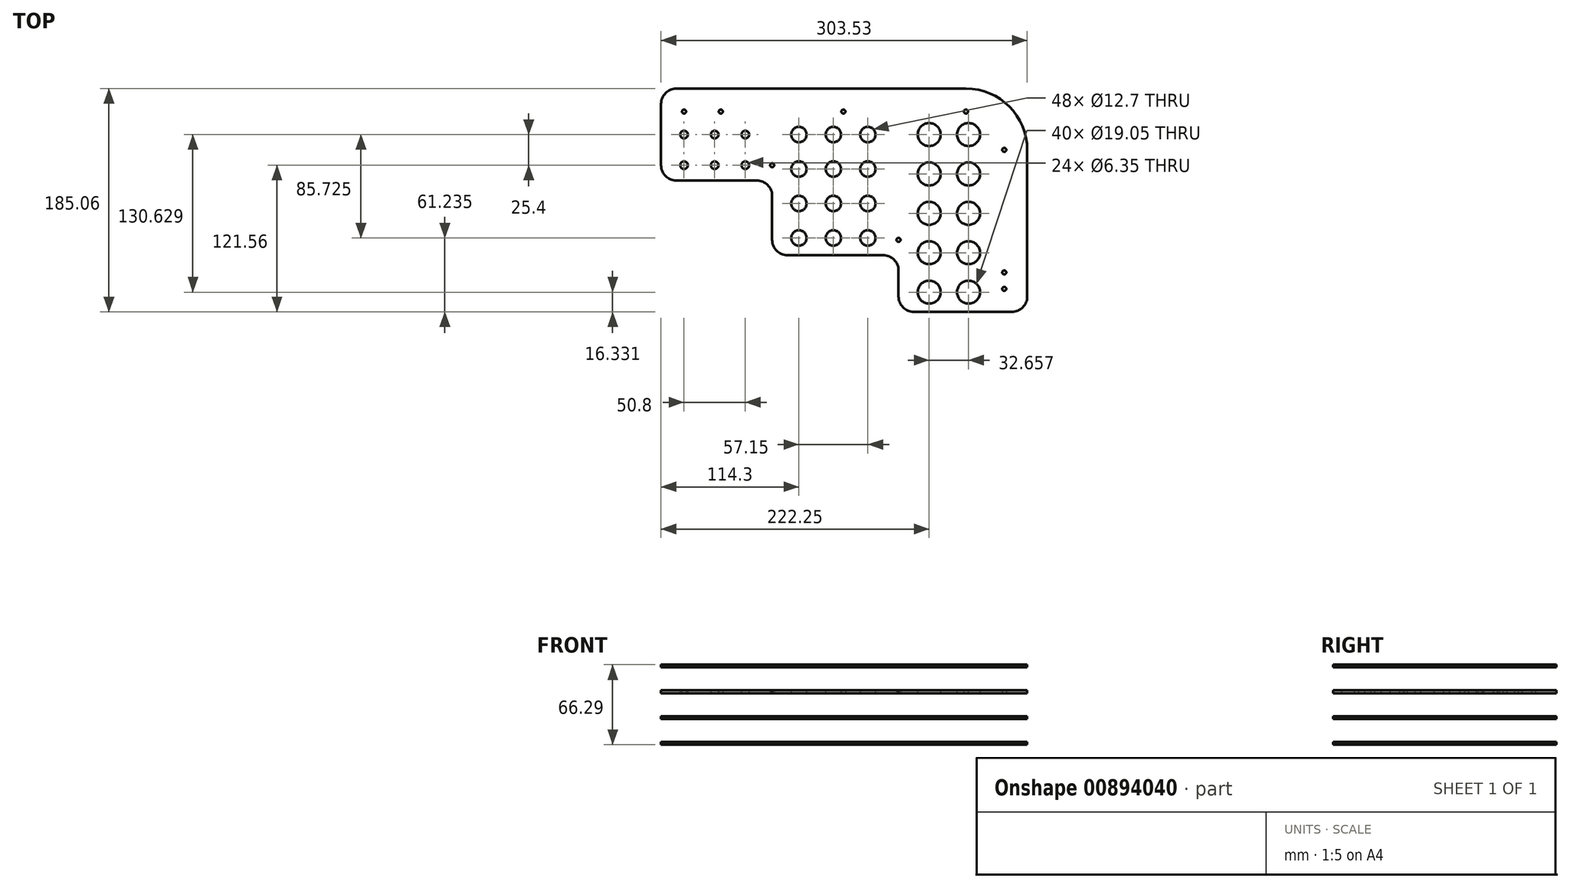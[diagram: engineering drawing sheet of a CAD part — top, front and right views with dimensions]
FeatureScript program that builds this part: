
annotation { "Feature Type Name" : "Feature", "Feature Type Description" : "" }
export const myFeature = defineFeature(function(context is Context, id is Id, definition is map)
    precondition{}
    {
        {
            var Q0;
            Q0=qCreatedBy(makeId("Top.planeOp"),FACE);
            var sketch = newSketch(context, id + "F0", { "sketchPlane" : qUnion([Q0])});
            skCircle(sketch, "E0", {"center": v(38.1, 38.1) * mm, "radius": 1.59 * mm});
            skCircle(sketch, "E1.0.1.0", {"center": v(38.1, 60.96) * mm, "radius": 1.59 * mm});
            skCircle(sketch, "E1.0.2.0", {"center": v(38.1, 83.82) * mm, "radius": 1.59 * mm});
            skCircle(sketch, "E1.0.3.0", {"center": v(38.1, 106.68) * mm, "radius": 1.59 * mm});
            skCircle(sketch, "E1.0.4.0", {"center": v(38.1, 129.54) * mm, "radius": 1.59 * mm});
            skCircle(sketch, "E1.0.5.0", {"center": v(38.1, 152.4) * mm, "radius": 1.59 * mm});
            skCircle(sketch, "E1.0.6.0", {"center": v(38.1, 175.26) * mm, "radius": 1.59 * mm});
            skCircle(sketch, "E1.0.7.0", {"center": v(38.1, 198.12) * mm, "radius": 1.59 * mm});
            skLineSegment(sketch, "E1.direction1", {"start": v(38.1, 38.1) * mm, "end": v(60.96, 38.1) * mm, "construction": true});
            skLineSegment(sketch, "E1.direction2", {"start": v(38.1, 38.1) * mm, "end": v(38.1, 60.96) * mm, "construction": true});
            skLineSegment(sketch, "E2.bottom", {"start": v(50.8, 304.8) * mm, "end": v(355.6, 304.8) * mm});
            skLineSegment(sketch, "E2.top", {"start": v(50.8, 0) * mm, "end": v(355.6, 0) * mm});
            skLineSegment(sketch, "E2.left", {"start": v(0, 254) * mm, "end": v(0, 50.8) * mm});
            skLineSegment(sketch, "E2.right", {"start": v(406.4, 254) * mm, "end": v(406.4, 50.8) * mm});
            skLineSegment(sketch, "E3.0", {"start": v(38.1, 266.7) * mm, "end": v(38.1, 38.1) * mm, "construction": true});
            skLineSegment(sketch, "E3.1", {"start": v(38.1, 266.7) * mm, "end": v(368.3, 266.7) * mm, "construction": true});
            skLineSegment(sketch, "E3.2", {"start": v(368.3, 266.7) * mm, "end": v(368.3, 38.1) * mm, "construction": true});
            skLineSegment(sketch, "E3.3", {"start": v(38.1, 38.1) * mm, "end": v(368.3, 38.1) * mm, "construction": true});
            skCircle(sketch, "E4.0.0.8", {"center": v(38.1, 220.98) * mm, "radius": 1.59 * mm});
            skCircle(sketch, "E4.0.0.9", {"center": v(38.1, 243.84) * mm, "radius": 1.59 * mm});
            skCircle(sketch, "E5.0.1.0", {"center": v(60.96, 38.1) * mm, "radius": 1.59 * mm});
            skCircle(sketch, "E5.0.1.1", {"center": v(60.96, 60.96) * mm, "radius": 1.59 * mm});
            skCircle(sketch, "E5.0.1.2", {"center": v(60.96, 83.82) * mm, "radius": 1.59 * mm});
            skCircle(sketch, "E5.0.1.3", {"center": v(60.96, 106.68) * mm, "radius": 1.59 * mm});
            skCircle(sketch, "E5.0.1.4", {"center": v(60.96, 129.54) * mm, "radius": 1.59 * mm});
            skCircle(sketch, "E5.0.1.5", {"center": v(60.96, 152.4) * mm, "radius": 1.59 * mm});
            skCircle(sketch, "E5.0.1.6", {"center": v(60.96, 175.26) * mm, "radius": 1.59 * mm});
            skCircle(sketch, "E5.0.1.7", {"center": v(60.96, 198.12) * mm, "radius": 1.59 * mm});
            skCircle(sketch, "E5.0.1.8", {"center": v(60.96, 220.98) * mm, "radius": 1.59 * mm});
            skCircle(sketch, "E5.0.1.9", {"center": v(60.96, 243.84) * mm, "radius": 1.59 * mm});
            skCircle(sketch, "E5.0.2.0", {"center": v(83.82, 38.1) * mm, "radius": 1.59 * mm});
            skCircle(sketch, "E5.0.2.1", {"center": v(83.82, 60.96) * mm, "radius": 1.59 * mm});
            skCircle(sketch, "E5.0.2.2", {"center": v(83.82, 83.82) * mm, "radius": 1.59 * mm});
            skCircle(sketch, "E5.0.2.3", {"center": v(83.82, 106.68) * mm, "radius": 1.59 * mm});
            skCircle(sketch, "E5.0.2.4", {"center": v(83.82, 129.54) * mm, "radius": 1.59 * mm});
            skCircle(sketch, "E5.0.2.5", {"center": v(83.82, 152.4) * mm, "radius": 1.59 * mm});
            skCircle(sketch, "E5.0.2.6", {"center": v(83.82, 175.26) * mm, "radius": 1.59 * mm});
            skCircle(sketch, "E5.0.2.7", {"center": v(83.82, 198.12) * mm, "radius": 1.59 * mm});
            skCircle(sketch, "E5.0.2.8", {"center": v(83.82, 220.98) * mm, "radius": 1.59 * mm});
            skCircle(sketch, "E5.0.2.9", {"center": v(83.82, 243.84) * mm, "radius": 1.59 * mm});
            skCircle(sketch, "E6.0.0.10", {"center": v(38.1, 266.7) * mm, "radius": 1.59 * mm});
            skCircle(sketch, "E6.0.1.10", {"center": v(60.96, 266.7) * mm, "radius": 1.59 * mm});
            skCircle(sketch, "E6.0.2.10", {"center": v(83.82, 266.7) * mm, "radius": 1.59 * mm});
            skCircle(sketch, "E7", {"center": v(121.92, 38.1) * mm, "radius": 3.18 * mm});
            skCircle(sketch, "E8.0.1.0", {"center": v(121.92, 63.5) * mm, "radius": 3.18 * mm});
            skCircle(sketch, "E8.0.2.0", {"center": v(121.92, 88.9) * mm, "radius": 3.18 * mm});
            skCircle(sketch, "E8.0.3.0", {"center": v(121.92, 114.3) * mm, "radius": 3.18 * mm});
            skCircle(sketch, "E8.0.4.0", {"center": v(121.92, 139.7) * mm, "radius": 3.18 * mm});
            skCircle(sketch, "E8.0.5.0", {"center": v(121.92, 165.1) * mm, "radius": 3.18 * mm});
            skCircle(sketch, "E8.0.6.0", {"center": v(121.92, 190.5) * mm, "radius": 3.18 * mm});
            skCircle(sketch, "E8.0.7.0", {"center": v(121.92, 215.9) * mm, "radius": 3.18 * mm});
            skCircle(sketch, "E8.0.8.0", {"center": v(121.92, 241.3) * mm, "radius": 3.18 * mm});
            skCircle(sketch, "E8.0.9.0", {"center": v(121.92, 266.7) * mm, "radius": 3.18 * mm});
            skCircle(sketch, "E8.1.0.0", {"center": v(147.32, 38.1) * mm, "radius": 3.18 * mm});
            skCircle(sketch, "E8.1.1.0", {"center": v(147.32, 63.5) * mm, "radius": 3.18 * mm});
            skCircle(sketch, "E8.1.2.0", {"center": v(147.32, 88.9) * mm, "radius": 3.18 * mm});
            skCircle(sketch, "E8.1.3.0", {"center": v(147.32, 114.3) * mm, "radius": 3.18 * mm});
            skCircle(sketch, "E8.1.4.0", {"center": v(147.32, 139.7) * mm, "radius": 3.18 * mm});
            skCircle(sketch, "E8.1.5.0", {"center": v(147.32, 165.1) * mm, "radius": 3.18 * mm});
            skCircle(sketch, "E8.1.6.0", {"center": v(147.32, 190.5) * mm, "radius": 3.18 * mm});
            skCircle(sketch, "E8.1.7.0", {"center": v(147.32, 215.9) * mm, "radius": 3.18 * mm});
            skCircle(sketch, "E8.1.8.0", {"center": v(147.32, 241.3) * mm, "radius": 3.18 * mm});
            skCircle(sketch, "E8.1.9.0", {"center": v(147.32, 266.7) * mm, "radius": 3.18 * mm});
            skCircle(sketch, "E8.2.0.0", {"center": v(172.72, 38.1) * mm, "radius": 3.18 * mm});
            skCircle(sketch, "E8.2.1.0", {"center": v(172.72, 63.5) * mm, "radius": 3.18 * mm});
            skCircle(sketch, "E8.2.2.0", {"center": v(172.72, 88.9) * mm, "radius": 3.18 * mm});
            skCircle(sketch, "E8.2.3.0", {"center": v(172.72, 114.3) * mm, "radius": 3.18 * mm});
            skCircle(sketch, "E8.2.4.0", {"center": v(172.72, 139.7) * mm, "radius": 3.18 * mm});
            skCircle(sketch, "E8.2.5.0", {"center": v(172.72, 165.1) * mm, "radius": 3.18 * mm});
            skCircle(sketch, "E8.2.6.0", {"center": v(172.72, 190.5) * mm, "radius": 3.18 * mm});
            skCircle(sketch, "E8.2.7.0", {"center": v(172.72, 215.9) * mm, "radius": 3.18 * mm});
            skCircle(sketch, "E8.2.8.0", {"center": v(172.72, 241.3) * mm, "radius": 3.18 * mm});
            skCircle(sketch, "E8.2.9.0", {"center": v(172.72, 266.7) * mm, "radius": 3.18 * mm});
            skLineSegment(sketch, "E8.direction1", {"start": v(121.92, 38.1) * mm, "end": v(147.32, 38.1) * mm, "construction": true});
            skLineSegment(sketch, "E8.direction2", {"start": v(121.92, 38.1) * mm, "end": v(121.92, 63.5) * mm, "construction": true});
            skCircle(sketch, "E9", {"center": v(217.17, 38.1) * mm, "radius": 6.35 * mm});
            skCircle(sketch, "E10.0.1.0", {"center": v(217.17, 66.67) * mm, "radius": 6.35 * mm});
            skCircle(sketch, "E10.0.2.0", {"center": v(217.17, 95.25) * mm, "radius": 6.35 * mm});
            skCircle(sketch, "E10.0.3.0", {"center": v(217.17, 123.82) * mm, "radius": 6.35 * mm});
            skCircle(sketch, "E10.0.4.0", {"center": v(217.17, 152.4) * mm, "radius": 6.35 * mm});
            skCircle(sketch, "E10.0.5.0", {"center": v(217.17, 180.97) * mm, "radius": 6.35 * mm});
            skCircle(sketch, "E10.0.6.0", {"center": v(217.17, 209.55) * mm, "radius": 6.35 * mm});
            skCircle(sketch, "E10.0.7.0", {"center": v(217.17, 238.12) * mm, "radius": 6.35 * mm});
            skCircle(sketch, "E10.0.8.0", {"center": v(217.17, 266.7) * mm, "radius": 6.35 * mm});
            skCircle(sketch, "E10.1.0.0", {"center": v(245.74, 38.1) * mm, "radius": 6.35 * mm});
            skCircle(sketch, "E10.1.1.0", {"center": v(245.74, 66.67) * mm, "radius": 6.35 * mm});
            skCircle(sketch, "E10.1.2.0", {"center": v(245.74, 95.25) * mm, "radius": 6.35 * mm});
            skCircle(sketch, "E10.1.3.0", {"center": v(245.74, 123.82) * mm, "radius": 6.35 * mm});
            skCircle(sketch, "E10.1.4.0", {"center": v(245.74, 152.4) * mm, "radius": 6.35 * mm});
            skCircle(sketch, "E10.1.5.0", {"center": v(245.74, 180.97) * mm, "radius": 6.35 * mm});
            skCircle(sketch, "E10.1.6.0", {"center": v(245.74, 209.55) * mm, "radius": 6.35 * mm});
            skCircle(sketch, "E10.1.7.0", {"center": v(245.74, 238.12) * mm, "radius": 6.35 * mm});
            skCircle(sketch, "E10.1.8.0", {"center": v(245.74, 266.7) * mm, "radius": 6.35 * mm});
            skCircle(sketch, "E10.2.0.0", {"center": v(274.32, 38.1) * mm, "radius": 6.35 * mm});
            skCircle(sketch, "E10.2.1.0", {"center": v(274.32, 66.67) * mm, "radius": 6.35 * mm});
            skCircle(sketch, "E10.2.2.0", {"center": v(274.32, 95.25) * mm, "radius": 6.35 * mm});
            skCircle(sketch, "E10.2.3.0", {"center": v(274.32, 123.82) * mm, "radius": 6.35 * mm});
            skCircle(sketch, "E10.2.4.0", {"center": v(274.32, 152.4) * mm, "radius": 6.35 * mm});
            skCircle(sketch, "E10.2.5.0", {"center": v(274.32, 180.97) * mm, "radius": 6.35 * mm});
            skCircle(sketch, "E10.2.6.0", {"center": v(274.32, 209.55) * mm, "radius": 6.35 * mm});
            skCircle(sketch, "E10.2.7.0", {"center": v(274.32, 238.12) * mm, "radius": 6.35 * mm});
            skCircle(sketch, "E10.2.8.0", {"center": v(274.32, 266.7) * mm, "radius": 6.35 * mm});
            skLineSegment(sketch, "E10.direction1", {"start": v(217.17, 38.1) * mm, "end": v(245.74, 38.1) * mm, "construction": true});
            skLineSegment(sketch, "E10.direction2", {"start": v(217.17, 38.1) * mm, "end": v(217.17, 66.67) * mm, "construction": true});
            skCircle(sketch, "E11", {"center": v(325.12, 38.1) * mm, "radius": 9.53 * mm});
            skCircle(sketch, "E12.0.1.0", {"center": v(325.12, 70.76) * mm, "radius": 9.53 * mm});
            skCircle(sketch, "E12.0.2.0", {"center": v(325.12, 103.41) * mm, "radius": 9.53 * mm});
            skCircle(sketch, "E12.0.3.0", {"center": v(325.12, 136.07) * mm, "radius": 9.53 * mm});
            skCircle(sketch, "E12.0.4.0", {"center": v(325.12, 168.73) * mm, "radius": 9.53 * mm});
            skCircle(sketch, "E12.0.5.0", {"center": v(325.12, 201.39) * mm, "radius": 9.53 * mm});
            skCircle(sketch, "E12.0.6.0", {"center": v(325.12, 234.04) * mm, "radius": 9.53 * mm});
            skCircle(sketch, "E12.0.7.0", {"center": v(325.12, 266.7) * mm, "radius": 9.53 * mm});
            skCircle(sketch, "E12.1.0.0", {"center": v(357.78, 38.1) * mm, "radius": 9.53 * mm});
            skCircle(sketch, "E12.1.1.0", {"center": v(357.78, 70.76) * mm, "radius": 9.53 * mm});
            skCircle(sketch, "E12.1.2.0", {"center": v(357.78, 103.41) * mm, "radius": 9.53 * mm});
            skCircle(sketch, "E12.1.3.0", {"center": v(357.78, 136.07) * mm, "radius": 9.53 * mm});
            skCircle(sketch, "E12.1.4.0", {"center": v(357.78, 168.73) * mm, "radius": 9.53 * mm});
            skCircle(sketch, "E12.1.5.0", {"center": v(357.78, 201.39) * mm, "radius": 9.53 * mm});
            skCircle(sketch, "E12.1.6.0", {"center": v(357.78, 234.04) * mm, "radius": 9.53 * mm});
            skCircle(sketch, "E12.1.7.0", {"center": v(357.78, 266.7) * mm, "radius": 9.53 * mm});
            skLineSegment(sketch, "E12.direction1", {"start": v(325.12, 38.1) * mm, "end": v(357.78, 38.1) * mm, "construction": true});
            skLineSegment(sketch, "E12.direction2", {"start": v(325.12, 38.1) * mm, "end": v(325.12, 70.76) * mm, "construction": true});
            skPoint(sketch, "E13.visualSharp", {"position": v(0, 304.8) * mm});
            skArc(sketch, "E13.filletArc", {"start": v(50.8, 304.8) * mm, "mid": v(14.88, 289.92) * mm, "end": v(0, 254) * mm});
            skPoint(sketch, "E14.visualSharp", {"position": v(406.4, 304.8) * mm});
            skArc(sketch, "E14.filletArc", {"start": v(406.4, 254) * mm, "mid": v(391.52, 289.92) * mm, "end": v(355.6, 304.8) * mm});
            skPoint(sketch, "E15.visualSharp", {"position": v(406.4, 0) * mm});
            skArc(sketch, "E15.filletArc", {"start": v(355.6, 0) * mm, "mid": v(391.52, 14.88) * mm, "end": v(406.4, 50.8) * mm});
            skPoint(sketch, "E16.visualSharp", {"position": v(0, 0) * mm});
            skArc(sketch, "E16.filletArc", {"start": v(0, 50.8) * mm, "mid": v(14.88, 14.88) * mm, "end": v(50.8, 0) * mm});
            skLineSegment(sketch, "E17.0", {"start": v(50.8, 285.75) * mm, "end": v(152.4, 285.75) * mm, "construction": true});
            skArc(sketch, "E17.1", {"start": v(387.35, 254) * mm, "mid": v(378.05, 276.45) * mm, "end": v(355.6, 285.75) * mm, "construction": true});
            skArc(sketch, "E17.2", {"start": v(50.8, 285.75) * mm, "mid": v(28.35, 276.45) * mm, "end": v(19.05, 254) * mm, "construction": true});
            skLineSegment(sketch, "E17.3", {"start": v(387.35, 254) * mm, "end": v(387.35, 50.8) * mm, "construction": true});
            skLineSegment(sketch, "E17.4", {"start": v(19.05, 254) * mm, "end": v(19.05, 50.8) * mm, "construction": true});
            skArc(sketch, "E17.5", {"start": v(19.05, 50.8) * mm, "mid": v(28.35, 28.35) * mm, "end": v(50.8, 19.05) * mm, "construction": true});
            skLineSegment(sketch, "E17.6", {"start": v(50.8, 19.05) * mm, "end": v(152.4, 19.05) * mm, "construction": true});
            skArc(sketch, "E17.7", {"start": v(355.6, 19.05) * mm, "mid": v(378.05, 28.35) * mm, "end": v(387.35, 50.8) * mm, "construction": true});
            skLineSegment(sketch, "E18", {"start": v(152.4, 285.75) * mm, "end": v(254, 285.75) * mm, "construction": true});
            skLineSegment(sketch, "E19", {"start": v(254, 285.75) * mm, "end": v(355.6, 285.75) * mm, "construction": true});
            skLineSegment(sketch, "E20", {"start": v(152.4, 19.05) * mm, "end": v(254, 19.05) * mm, "construction": true});
            skLineSegment(sketch, "E21", {"start": v(254, 19.05) * mm, "end": v(355.6, 19.05) * mm, "construction": true});
            skCircle(sketch, "E22", {"center": v(50.8, 285.75) * mm, "radius": 1.65 * mm});
            skCircle(sketch, "E23", {"center": v(152.4, 285.75) * mm, "radius": 1.65 * mm});
            skCircle(sketch, "E24", {"center": v(254, 285.75) * mm, "radius": 1.65 * mm});
            skCircle(sketch, "E25", {"center": v(355.6, 285.75) * mm, "radius": 1.65 * mm});
            skCircle(sketch, "E26", {"center": v(19.05, 254) * mm, "radius": 1.65 * mm});
            skCircle(sketch, "E27", {"center": v(19.05, 152.4) * mm, "radius": 1.65 * mm});
            skCircle(sketch, "E28", {"center": v(19.05, 50.8) * mm, "radius": 1.65 * mm});
            skCircle(sketch, "E29", {"center": v(50.8, 19.05) * mm, "radius": 1.65 * mm});
            skCircle(sketch, "E30", {"center": v(152.4, 19.05) * mm, "radius": 1.65 * mm});
            skCircle(sketch, "E31", {"center": v(254, 19.05) * mm, "radius": 1.65 * mm});
            skCircle(sketch, "E32", {"center": v(355.6, 19.05) * mm, "radius": 1.65 * mm});
            skCircle(sketch, "E33", {"center": v(387.35, 50.8) * mm, "radius": 1.65 * mm});
            skCircle(sketch, "E34", {"center": v(387.35, 152.4) * mm, "radius": 1.65 * mm});
            skCircle(sketch, "E35", {"center": v(387.35, 254) * mm, "radius": 1.65 * mm});
            skPoint(sketch, "E36", {"position": v(203.2, 285.75) * mm});
            skSolve(sketch);
        }
        {
            var Q0;
            Q0=makeQuery(id+"F0.imprint","IMPRINT",FACE,{"disambiguationData":[TD([[makeQuery(id+"F0.imprint","IMPRINT",EDGE,{"derivedFrom":sQuery(id+"F0.wireOp",EDGE,"E0")}),-1.0]])]});
            extrude(context, id + "F1", {"entities" : qUnion([Q0]), "depth" : 2.3 * mm, "offsetDistance" : 25.4 * mm});
        }
        {
            var Q0;
            Q0=makeQuery(id+"F1.opExtrude","SWEPT_BODY",BODY,{"disambiguationData":[OSD([sQuery(id+"F0.wireOp",EDGE,"E0"),sQuery(id+"F0.wireOp",EDGE,"E1.0.1.0"),sQuery(id+"F0.wireOp",EDGE,"E1.0.2.0"),sQuery(id+"F0.wireOp",EDGE,"E1.0.3.0"),sQuery(id+"F0.wireOp",EDGE,"E1.0.4.0"),sQuery(id+"F0.wireOp",EDGE,"E1.0.5.0"),sQuery(id+"F0.wireOp",EDGE,"E1.0.6.0"),sQuery(id+"F0.wireOp",EDGE,"E1.0.7.0"),sQuery(id+"F0.wireOp",EDGE,"E2.bottom"),sQuery(id+"F0.wireOp",EDGE,"E2.top"),sQuery(id+"F0.wireOp",EDGE,"E2.left"),sQuery(id+"F0.wireOp",EDGE,"E2.right"),sQuery(id+"F0.wireOp",EDGE,"E4.0.0.8"),sQuery(id+"F0.wireOp",EDGE,"E4.0.0.9"),sQuery(id+"F0.wireOp",EDGE,"E5.0.1.0"),sQuery(id+"F0.wireOp",EDGE,"E5.0.1.1"),sQuery(id+"F0.wireOp",EDGE,"E5.0.1.2"),sQuery(id+"F0.wireOp",EDGE,"E5.0.1.3"),sQuery(id+"F0.wireOp",EDGE,"E5.0.1.4"),sQuery(id+"F0.wireOp",EDGE,"E5.0.1.5"),sQuery(id+"F0.wireOp",EDGE,"E5.0.1.6"),sQuery(id+"F0.wireOp",EDGE,"E5.0.1.7"),sQuery(id+"F0.wireOp",EDGE,"E5.0.1.8"),sQuery(id+"F0.wireOp",EDGE,"E5.0.1.9"),sQuery(id+"F0.wireOp",EDGE,"E5.0.2.0"),sQuery(id+"F0.wireOp",EDGE,"E5.0.2.1"),sQuery(id+"F0.wireOp",EDGE,"E5.0.2.2"),sQuery(id+"F0.wireOp",EDGE,"E5.0.2.3"),sQuery(id+"F0.wireOp",EDGE,"E5.0.2.4"),sQuery(id+"F0.wireOp",EDGE,"E5.0.2.5"),sQuery(id+"F0.wireOp",EDGE,"E5.0.2.6"),sQuery(id+"F0.wireOp",EDGE,"E5.0.2.7"),sQuery(id+"F0.wireOp",EDGE,"E5.0.2.8"),sQuery(id+"F0.wireOp",EDGE,"E5.0.2.9"),sQuery(id+"F0.wireOp",EDGE,"E6.0.0.10"),sQuery(id+"F0.wireOp",EDGE,"E6.0.1.10"),sQuery(id+"F0.wireOp",EDGE,"E6.0.2.10"),sQuery(id+"F0.wireOp",EDGE,"E7"),sQuery(id+"F0.wireOp",EDGE,"E8.0.1.0"),sQuery(id+"F0.wireOp",EDGE,"E8.0.2.0"),sQuery(id+"F0.wireOp",EDGE,"E8.0.3.0"),sQuery(id+"F0.wireOp",EDGE,"E8.0.4.0"),sQuery(id+"F0.wireOp",EDGE,"E8.0.5.0"),sQuery(id+"F0.wireOp",EDGE,"E8.0.6.0"),sQuery(id+"F0.wireOp",EDGE,"E8.0.7.0"),sQuery(id+"F0.wireOp",EDGE,"E8.0.8.0"),sQuery(id+"F0.wireOp",EDGE,"E8.0.9.0"),sQuery(id+"F0.wireOp",EDGE,"E8.1.0.0"),sQuery(id+"F0.wireOp",EDGE,"E8.1.1.0"),sQuery(id+"F0.wireOp",EDGE,"E8.1.2.0"),sQuery(id+"F0.wireOp",EDGE,"E8.1.3.0"),sQuery(id+"F0.wireOp",EDGE,"E8.1.4.0"),sQuery(id+"F0.wireOp",EDGE,"E8.1.5.0"),sQuery(id+"F0.wireOp",EDGE,"E8.1.6.0"),sQuery(id+"F0.wireOp",EDGE,"E8.1.7.0"),sQuery(id+"F0.wireOp",EDGE,"E8.1.8.0"),sQuery(id+"F0.wireOp",EDGE,"E8.1.9.0"),sQuery(id+"F0.wireOp",EDGE,"E8.2.0.0"),sQuery(id+"F0.wireOp",EDGE,"E8.2.1.0"),sQuery(id+"F0.wireOp",EDGE,"E8.2.2.0"),sQuery(id+"F0.wireOp",EDGE,"E8.2.3.0"),sQuery(id+"F0.wireOp",EDGE,"E8.2.4.0"),sQuery(id+"F0.wireOp",EDGE,"E8.2.5.0"),sQuery(id+"F0.wireOp",EDGE,"E8.2.6.0"),sQuery(id+"F0.wireOp",EDGE,"E8.2.7.0"),sQuery(id+"F0.wireOp",EDGE,"E8.2.8.0"),sQuery(id+"F0.wireOp",EDGE,"E8.2.9.0"),sQuery(id+"F0.wireOp",EDGE,"E9"),sQuery(id+"F0.wireOp",EDGE,"E10.0.1.0"),sQuery(id+"F0.wireOp",EDGE,"E10.0.2.0"),sQuery(id+"F0.wireOp",EDGE,"E10.0.3.0"),sQuery(id+"F0.wireOp",EDGE,"E10.0.4.0"),sQuery(id+"F0.wireOp",EDGE,"E10.0.5.0"),sQuery(id+"F0.wireOp",EDGE,"E10.0.6.0"),sQuery(id+"F0.wireOp",EDGE,"E10.0.7.0"),sQuery(id+"F0.wireOp",EDGE,"E10.0.8.0"),sQuery(id+"F0.wireOp",EDGE,"E10.1.0.0"),sQuery(id+"F0.wireOp",EDGE,"E10.1.1.0"),sQuery(id+"F0.wireOp",EDGE,"E10.1.2.0"),sQuery(id+"F0.wireOp",EDGE,"E10.1.3.0"),sQuery(id+"F0.wireOp",EDGE,"E10.1.4.0"),sQuery(id+"F0.wireOp",EDGE,"E10.1.5.0"),sQuery(id+"F0.wireOp",EDGE,"E10.1.6.0"),sQuery(id+"F0.wireOp",EDGE,"E10.1.7.0"),sQuery(id+"F0.wireOp",EDGE,"E10.1.8.0"),sQuery(id+"F0.wireOp",EDGE,"E10.2.0.0"),sQuery(id+"F0.wireOp",EDGE,"E10.2.1.0"),sQuery(id+"F0.wireOp",EDGE,"E10.2.2.0"),sQuery(id+"F0.wireOp",EDGE,"E10.2.3.0"),sQuery(id+"F0.wireOp",EDGE,"E10.2.4.0"),sQuery(id+"F0.wireOp",EDGE,"E10.2.5.0"),sQuery(id+"F0.wireOp",EDGE,"E10.2.6.0"),sQuery(id+"F0.wireOp",EDGE,"E10.2.7.0"),sQuery(id+"F0.wireOp",EDGE,"E10.2.8.0"),sQuery(id+"F0.wireOp",EDGE,"E11"),sQuery(id+"F0.wireOp",EDGE,"E12.0.1.0"),sQuery(id+"F0.wireOp",EDGE,"E12.0.2.0"),sQuery(id+"F0.wireOp",EDGE,"E12.0.3.0"),sQuery(id+"F0.wireOp",EDGE,"E12.0.4.0"),sQuery(id+"F0.wireOp",EDGE,"E12.0.5.0"),sQuery(id+"F0.wireOp",EDGE,"E12.0.6.0"),sQuery(id+"F0.wireOp",EDGE,"E12.0.7.0"),sQuery(id+"F0.wireOp",EDGE,"E12.1.0.0"),sQuery(id+"F0.wireOp",EDGE,"E12.1.1.0"),sQuery(id+"F0.wireOp",EDGE,"E12.1.2.0"),sQuery(id+"F0.wireOp",EDGE,"E12.1.3.0"),sQuery(id+"F0.wireOp",EDGE,"E12.1.4.0"),sQuery(id+"F0.wireOp",EDGE,"E12.1.5.0"),sQuery(id+"F0.wireOp",EDGE,"E12.1.6.0"),sQuery(id+"F0.wireOp",EDGE,"E12.1.7.0"),sQuery(id+"F0.wireOp",EDGE,"E13.filletArc"),sQuery(id+"F0.wireOp",EDGE,"E14.filletArc"),sQuery(id+"F0.wireOp",EDGE,"E15.filletArc"),sQuery(id+"F0.wireOp",EDGE,"E16.filletArc")])]});
            transform(context, id + "F2", {"entities" : qUnion([Q0]), "transformType" : TransformType.TRANSLATION_3D, "dx" : 0 * mm, "dy" : 0 * mm, "dz" : 21.34 * mm, "makeCopy" : true});
        }
        {
            var Q0;
            Q0=makeQuery(id+"F2.opPattern","COPY",BODY,{"derivedFrom":makeQuery(id+"F1.opExtrude","SWEPT_BODY",BODY,{"disambiguationData":[OSD([sQuery(id+"F0.wireOp",EDGE,"E0"),sQuery(id+"F0.wireOp",EDGE,"E1.0.1.0"),sQuery(id+"F0.wireOp",EDGE,"E1.0.2.0"),sQuery(id+"F0.wireOp",EDGE,"E1.0.3.0"),sQuery(id+"F0.wireOp",EDGE,"E1.0.4.0"),sQuery(id+"F0.wireOp",EDGE,"E1.0.5.0"),sQuery(id+"F0.wireOp",EDGE,"E1.0.6.0"),sQuery(id+"F0.wireOp",EDGE,"E1.0.7.0"),sQuery(id+"F0.wireOp",EDGE,"E2.bottom"),sQuery(id+"F0.wireOp",EDGE,"E2.top"),sQuery(id+"F0.wireOp",EDGE,"E2.left"),sQuery(id+"F0.wireOp",EDGE,"E2.right"),sQuery(id+"F0.wireOp",EDGE,"E4.0.0.8"),sQuery(id+"F0.wireOp",EDGE,"E4.0.0.9"),sQuery(id+"F0.wireOp",EDGE,"E5.0.1.0"),sQuery(id+"F0.wireOp",EDGE,"E5.0.1.1"),sQuery(id+"F0.wireOp",EDGE,"E5.0.1.2"),sQuery(id+"F0.wireOp",EDGE,"E5.0.1.3"),sQuery(id+"F0.wireOp",EDGE,"E5.0.1.4"),sQuery(id+"F0.wireOp",EDGE,"E5.0.1.5"),sQuery(id+"F0.wireOp",EDGE,"E5.0.1.6"),sQuery(id+"F0.wireOp",EDGE,"E5.0.1.7"),sQuery(id+"F0.wireOp",EDGE,"E5.0.1.8"),sQuery(id+"F0.wireOp",EDGE,"E5.0.1.9"),sQuery(id+"F0.wireOp",EDGE,"E5.0.2.0"),sQuery(id+"F0.wireOp",EDGE,"E5.0.2.1"),sQuery(id+"F0.wireOp",EDGE,"E5.0.2.2"),sQuery(id+"F0.wireOp",EDGE,"E5.0.2.3"),sQuery(id+"F0.wireOp",EDGE,"E5.0.2.4"),sQuery(id+"F0.wireOp",EDGE,"E5.0.2.5"),sQuery(id+"F0.wireOp",EDGE,"E5.0.2.6"),sQuery(id+"F0.wireOp",EDGE,"E5.0.2.7"),sQuery(id+"F0.wireOp",EDGE,"E5.0.2.8"),sQuery(id+"F0.wireOp",EDGE,"E5.0.2.9"),sQuery(id+"F0.wireOp",EDGE,"E6.0.0.10"),sQuery(id+"F0.wireOp",EDGE,"E6.0.1.10"),sQuery(id+"F0.wireOp",EDGE,"E6.0.2.10"),sQuery(id+"F0.wireOp",EDGE,"E7"),sQuery(id+"F0.wireOp",EDGE,"E8.0.1.0"),sQuery(id+"F0.wireOp",EDGE,"E8.0.2.0"),sQuery(id+"F0.wireOp",EDGE,"E8.0.3.0"),sQuery(id+"F0.wireOp",EDGE,"E8.0.4.0"),sQuery(id+"F0.wireOp",EDGE,"E8.0.5.0"),sQuery(id+"F0.wireOp",EDGE,"E8.0.6.0"),sQuery(id+"F0.wireOp",EDGE,"E8.0.7.0"),sQuery(id+"F0.wireOp",EDGE,"E8.0.8.0"),sQuery(id+"F0.wireOp",EDGE,"E8.0.9.0"),sQuery(id+"F0.wireOp",EDGE,"E8.1.0.0"),sQuery(id+"F0.wireOp",EDGE,"E8.1.1.0"),sQuery(id+"F0.wireOp",EDGE,"E8.1.2.0"),sQuery(id+"F0.wireOp",EDGE,"E8.1.3.0"),sQuery(id+"F0.wireOp",EDGE,"E8.1.4.0"),sQuery(id+"F0.wireOp",EDGE,"E8.1.5.0"),sQuery(id+"F0.wireOp",EDGE,"E8.1.6.0"),sQuery(id+"F0.wireOp",EDGE,"E8.1.7.0"),sQuery(id+"F0.wireOp",EDGE,"E8.1.8.0"),sQuery(id+"F0.wireOp",EDGE,"E8.1.9.0"),sQuery(id+"F0.wireOp",EDGE,"E8.2.0.0"),sQuery(id+"F0.wireOp",EDGE,"E8.2.1.0"),sQuery(id+"F0.wireOp",EDGE,"E8.2.2.0"),sQuery(id+"F0.wireOp",EDGE,"E8.2.3.0"),sQuery(id+"F0.wireOp",EDGE,"E8.2.4.0"),sQuery(id+"F0.wireOp",EDGE,"E8.2.5.0"),sQuery(id+"F0.wireOp",EDGE,"E8.2.6.0"),sQuery(id+"F0.wireOp",EDGE,"E8.2.7.0"),sQuery(id+"F0.wireOp",EDGE,"E8.2.8.0"),sQuery(id+"F0.wireOp",EDGE,"E8.2.9.0"),sQuery(id+"F0.wireOp",EDGE,"E9"),sQuery(id+"F0.wireOp",EDGE,"E10.0.1.0"),sQuery(id+"F0.wireOp",EDGE,"E10.0.2.0"),sQuery(id+"F0.wireOp",EDGE,"E10.0.3.0"),sQuery(id+"F0.wireOp",EDGE,"E10.0.4.0"),sQuery(id+"F0.wireOp",EDGE,"E10.0.5.0"),sQuery(id+"F0.wireOp",EDGE,"E10.0.6.0"),sQuery(id+"F0.wireOp",EDGE,"E10.0.7.0"),sQuery(id+"F0.wireOp",EDGE,"E10.0.8.0"),sQuery(id+"F0.wireOp",EDGE,"E10.1.0.0"),sQuery(id+"F0.wireOp",EDGE,"E10.1.1.0"),sQuery(id+"F0.wireOp",EDGE,"E10.1.2.0"),sQuery(id+"F0.wireOp",EDGE,"E10.1.3.0"),sQuery(id+"F0.wireOp",EDGE,"E10.1.4.0"),sQuery(id+"F0.wireOp",EDGE,"E10.1.5.0"),sQuery(id+"F0.wireOp",EDGE,"E10.1.6.0"),sQuery(id+"F0.wireOp",EDGE,"E10.1.7.0"),sQuery(id+"F0.wireOp",EDGE,"E10.1.8.0"),sQuery(id+"F0.wireOp",EDGE,"E10.2.0.0"),sQuery(id+"F0.wireOp",EDGE,"E10.2.1.0"),sQuery(id+"F0.wireOp",EDGE,"E10.2.2.0"),sQuery(id+"F0.wireOp",EDGE,"E10.2.3.0"),sQuery(id+"F0.wireOp",EDGE,"E10.2.4.0"),sQuery(id+"F0.wireOp",EDGE,"E10.2.5.0"),sQuery(id+"F0.wireOp",EDGE,"E10.2.6.0"),sQuery(id+"F0.wireOp",EDGE,"E10.2.7.0"),sQuery(id+"F0.wireOp",EDGE,"E10.2.8.0"),sQuery(id+"F0.wireOp",EDGE,"E11"),sQuery(id+"F0.wireOp",EDGE,"E12.0.1.0"),sQuery(id+"F0.wireOp",EDGE,"E12.0.2.0"),sQuery(id+"F0.wireOp",EDGE,"E12.0.3.0"),sQuery(id+"F0.wireOp",EDGE,"E12.0.4.0"),sQuery(id+"F0.wireOp",EDGE,"E12.0.5.0"),sQuery(id+"F0.wireOp",EDGE,"E12.0.6.0"),sQuery(id+"F0.wireOp",EDGE,"E12.0.7.0"),sQuery(id+"F0.wireOp",EDGE,"E12.1.0.0"),sQuery(id+"F0.wireOp",EDGE,"E12.1.1.0"),sQuery(id+"F0.wireOp",EDGE,"E12.1.2.0"),sQuery(id+"F0.wireOp",EDGE,"E12.1.3.0"),sQuery(id+"F0.wireOp",EDGE,"E12.1.4.0"),sQuery(id+"F0.wireOp",EDGE,"E12.1.5.0"),sQuery(id+"F0.wireOp",EDGE,"E12.1.6.0"),sQuery(id+"F0.wireOp",EDGE,"E12.1.7.0"),sQuery(id+"F0.wireOp",EDGE,"E13.filletArc"),sQuery(id+"F0.wireOp",EDGE,"E14.filletArc"),sQuery(id+"F0.wireOp",EDGE,"E15.filletArc"),sQuery(id+"F0.wireOp",EDGE,"E16.filletArc")])]}),"instanceName":"1"});
            transform(context, id + "F3", {"entities" : qUnion([Q0]), "transformType" : TransformType.TRANSLATION_3D, "dx" : 0 * mm, "dy" : 0 * mm, "dz" : 21.34 * mm, "makeCopy" : true});
        }
        {
            var Q0;
            Q0=makeQuery(id+"F3.opPattern","COPY",BODY,{"derivedFrom":makeQuery(id+"F2.opPattern","COPY",BODY,{"derivedFrom":makeQuery(id+"F1.opExtrude","SWEPT_BODY",BODY,{"disambiguationData":[OSD([sQuery(id+"F0.wireOp",EDGE,"E0"),sQuery(id+"F0.wireOp",EDGE,"E1.0.1.0"),sQuery(id+"F0.wireOp",EDGE,"E1.0.2.0"),sQuery(id+"F0.wireOp",EDGE,"E1.0.3.0"),sQuery(id+"F0.wireOp",EDGE,"E1.0.4.0"),sQuery(id+"F0.wireOp",EDGE,"E1.0.5.0"),sQuery(id+"F0.wireOp",EDGE,"E1.0.6.0"),sQuery(id+"F0.wireOp",EDGE,"E1.0.7.0"),sQuery(id+"F0.wireOp",EDGE,"E2.bottom"),sQuery(id+"F0.wireOp",EDGE,"E2.top"),sQuery(id+"F0.wireOp",EDGE,"E2.left"),sQuery(id+"F0.wireOp",EDGE,"E2.right"),sQuery(id+"F0.wireOp",EDGE,"E4.0.0.8"),sQuery(id+"F0.wireOp",EDGE,"E4.0.0.9"),sQuery(id+"F0.wireOp",EDGE,"E5.0.1.0"),sQuery(id+"F0.wireOp",EDGE,"E5.0.1.1"),sQuery(id+"F0.wireOp",EDGE,"E5.0.1.2"),sQuery(id+"F0.wireOp",EDGE,"E5.0.1.3"),sQuery(id+"F0.wireOp",EDGE,"E5.0.1.4"),sQuery(id+"F0.wireOp",EDGE,"E5.0.1.5"),sQuery(id+"F0.wireOp",EDGE,"E5.0.1.6"),sQuery(id+"F0.wireOp",EDGE,"E5.0.1.7"),sQuery(id+"F0.wireOp",EDGE,"E5.0.1.8"),sQuery(id+"F0.wireOp",EDGE,"E5.0.1.9"),sQuery(id+"F0.wireOp",EDGE,"E5.0.2.0"),sQuery(id+"F0.wireOp",EDGE,"E5.0.2.1"),sQuery(id+"F0.wireOp",EDGE,"E5.0.2.2"),sQuery(id+"F0.wireOp",EDGE,"E5.0.2.3"),sQuery(id+"F0.wireOp",EDGE,"E5.0.2.4"),sQuery(id+"F0.wireOp",EDGE,"E5.0.2.5"),sQuery(id+"F0.wireOp",EDGE,"E5.0.2.6"),sQuery(id+"F0.wireOp",EDGE,"E5.0.2.7"),sQuery(id+"F0.wireOp",EDGE,"E5.0.2.8"),sQuery(id+"F0.wireOp",EDGE,"E5.0.2.9"),sQuery(id+"F0.wireOp",EDGE,"E6.0.0.10"),sQuery(id+"F0.wireOp",EDGE,"E6.0.1.10"),sQuery(id+"F0.wireOp",EDGE,"E6.0.2.10"),sQuery(id+"F0.wireOp",EDGE,"E7"),sQuery(id+"F0.wireOp",EDGE,"E8.0.1.0"),sQuery(id+"F0.wireOp",EDGE,"E8.0.2.0"),sQuery(id+"F0.wireOp",EDGE,"E8.0.3.0"),sQuery(id+"F0.wireOp",EDGE,"E8.0.4.0"),sQuery(id+"F0.wireOp",EDGE,"E8.0.5.0"),sQuery(id+"F0.wireOp",EDGE,"E8.0.6.0"),sQuery(id+"F0.wireOp",EDGE,"E8.0.7.0"),sQuery(id+"F0.wireOp",EDGE,"E8.0.8.0"),sQuery(id+"F0.wireOp",EDGE,"E8.0.9.0"),sQuery(id+"F0.wireOp",EDGE,"E8.1.0.0"),sQuery(id+"F0.wireOp",EDGE,"E8.1.1.0"),sQuery(id+"F0.wireOp",EDGE,"E8.1.2.0"),sQuery(id+"F0.wireOp",EDGE,"E8.1.3.0"),sQuery(id+"F0.wireOp",EDGE,"E8.1.4.0"),sQuery(id+"F0.wireOp",EDGE,"E8.1.5.0"),sQuery(id+"F0.wireOp",EDGE,"E8.1.6.0"),sQuery(id+"F0.wireOp",EDGE,"E8.1.7.0"),sQuery(id+"F0.wireOp",EDGE,"E8.1.8.0"),sQuery(id+"F0.wireOp",EDGE,"E8.1.9.0"),sQuery(id+"F0.wireOp",EDGE,"E8.2.0.0"),sQuery(id+"F0.wireOp",EDGE,"E8.2.1.0"),sQuery(id+"F0.wireOp",EDGE,"E8.2.2.0"),sQuery(id+"F0.wireOp",EDGE,"E8.2.3.0"),sQuery(id+"F0.wireOp",EDGE,"E8.2.4.0"),sQuery(id+"F0.wireOp",EDGE,"E8.2.5.0"),sQuery(id+"F0.wireOp",EDGE,"E8.2.6.0"),sQuery(id+"F0.wireOp",EDGE,"E8.2.7.0"),sQuery(id+"F0.wireOp",EDGE,"E8.2.8.0"),sQuery(id+"F0.wireOp",EDGE,"E8.2.9.0"),sQuery(id+"F0.wireOp",EDGE,"E9"),sQuery(id+"F0.wireOp",EDGE,"E10.0.1.0"),sQuery(id+"F0.wireOp",EDGE,"E10.0.2.0"),sQuery(id+"F0.wireOp",EDGE,"E10.0.3.0"),sQuery(id+"F0.wireOp",EDGE,"E10.0.4.0"),sQuery(id+"F0.wireOp",EDGE,"E10.0.5.0"),sQuery(id+"F0.wireOp",EDGE,"E10.0.6.0"),sQuery(id+"F0.wireOp",EDGE,"E10.0.7.0"),sQuery(id+"F0.wireOp",EDGE,"E10.0.8.0"),sQuery(id+"F0.wireOp",EDGE,"E10.1.0.0"),sQuery(id+"F0.wireOp",EDGE,"E10.1.1.0"),sQuery(id+"F0.wireOp",EDGE,"E10.1.2.0"),sQuery(id+"F0.wireOp",EDGE,"E10.1.3.0"),sQuery(id+"F0.wireOp",EDGE,"E10.1.4.0"),sQuery(id+"F0.wireOp",EDGE,"E10.1.5.0"),sQuery(id+"F0.wireOp",EDGE,"E10.1.6.0"),sQuery(id+"F0.wireOp",EDGE,"E10.1.7.0"),sQuery(id+"F0.wireOp",EDGE,"E10.1.8.0"),sQuery(id+"F0.wireOp",EDGE,"E10.2.0.0"),sQuery(id+"F0.wireOp",EDGE,"E10.2.1.0"),sQuery(id+"F0.wireOp",EDGE,"E10.2.2.0"),sQuery(id+"F0.wireOp",EDGE,"E10.2.3.0"),sQuery(id+"F0.wireOp",EDGE,"E10.2.4.0"),sQuery(id+"F0.wireOp",EDGE,"E10.2.5.0"),sQuery(id+"F0.wireOp",EDGE,"E10.2.6.0"),sQuery(id+"F0.wireOp",EDGE,"E10.2.7.0"),sQuery(id+"F0.wireOp",EDGE,"E10.2.8.0"),sQuery(id+"F0.wireOp",EDGE,"E11"),sQuery(id+"F0.wireOp",EDGE,"E12.0.1.0"),sQuery(id+"F0.wireOp",EDGE,"E12.0.2.0"),sQuery(id+"F0.wireOp",EDGE,"E12.0.3.0"),sQuery(id+"F0.wireOp",EDGE,"E12.0.4.0"),sQuery(id+"F0.wireOp",EDGE,"E12.0.5.0"),sQuery(id+"F0.wireOp",EDGE,"E12.0.6.0"),sQuery(id+"F0.wireOp",EDGE,"E12.0.7.0"),sQuery(id+"F0.wireOp",EDGE,"E12.1.0.0"),sQuery(id+"F0.wireOp",EDGE,"E12.1.1.0"),sQuery(id+"F0.wireOp",EDGE,"E12.1.2.0"),sQuery(id+"F0.wireOp",EDGE,"E12.1.3.0"),sQuery(id+"F0.wireOp",EDGE,"E12.1.4.0"),sQuery(id+"F0.wireOp",EDGE,"E12.1.5.0"),sQuery(id+"F0.wireOp",EDGE,"E12.1.6.0"),sQuery(id+"F0.wireOp",EDGE,"E12.1.7.0"),sQuery(id+"F0.wireOp",EDGE,"E13.filletArc"),sQuery(id+"F0.wireOp",EDGE,"E14.filletArc"),sQuery(id+"F0.wireOp",EDGE,"E15.filletArc"),sQuery(id+"F0.wireOp",EDGE,"E16.filletArc")])]}),"instanceName":"1"}),"instanceName":"1"});
            transform(context, id + "F4", {"entities" : qUnion([Q0]), "transformType" : TransformType.TRANSLATION_3D, "dx" : 0 * mm, "dy" : 0 * mm, "dz" : 21.34 * mm, "makeCopy" : true});
        }
        {
            var Q0;
            Q0=qCreatedBy(makeId("Top.planeOp"),FACE);
            var sketch = newSketch(context, id + "F5", { "sketchPlane" : qUnion([Q0])});
            skCircle(sketch, "E37", {"center": v(38.1, 38.1) * mm, "radius": 1.59 * mm, "construction": true});
            skCircle(sketch, "E38.0.1.0", {"center": v(38.1, 60.96) * mm, "radius": 1.59 * mm, "construction": true});
            skCircle(sketch, "E38.0.2.0", {"center": v(38.1, 83.82) * mm, "radius": 1.59 * mm, "construction": true});
            skCircle(sketch, "E38.0.3.0", {"center": v(38.1, 106.68) * mm, "radius": 1.59 * mm, "construction": true});
            skCircle(sketch, "E38.0.4.0", {"center": v(38.1, 129.54) * mm, "radius": 1.59 * mm, "construction": true});
            skCircle(sketch, "E38.0.5.0", {"center": v(38.1, 152.4) * mm, "radius": 1.59 * mm, "construction": true});
            skCircle(sketch, "E38.0.6.0", {"center": v(38.1, 175.26) * mm, "radius": 1.59 * mm, "construction": true});
            skCircle(sketch, "E38.0.7.0", {"center": v(38.1, 198.12) * mm, "radius": 1.59 * mm, "construction": true});
            skLineSegment(sketch, "E38.direction1", {"start": v(38.1, 38.1) * mm, "end": v(60.96, 38.1) * mm, "construction": true});
            skLineSegment(sketch, "E38.direction2", {"start": v(38.1, 38.1) * mm, "end": v(38.1, 60.96) * mm, "construction": true});
            skLineSegment(sketch, "E39.bottom", {"start": v(50.8, 304.8) * mm, "end": v(355.6, 304.8) * mm});
            skLineSegment(sketch, "E39.top", {"start": v(312.42, 0) * mm, "end": v(355.6, 0) * mm});
            skLineSegment(sketch, "E39.left", {"start": v(0, 254) * mm, "end": v(0, 176.53) * mm});
            skLineSegment(sketch, "E39.right", {"start": v(406.4, 254) * mm, "end": v(406.4, 50.8) * mm});
            skLineSegment(sketch, "E40.0", {"start": v(38.1, 266.7) * mm, "end": v(38.1, 38.1) * mm, "construction": true});
            skLineSegment(sketch, "E40.1", {"start": v(38.1, 266.7) * mm, "end": v(368.3, 266.7) * mm, "construction": true});
            skLineSegment(sketch, "E40.2", {"start": v(368.3, 266.7) * mm, "end": v(368.3, 38.1) * mm, "construction": true});
            skLineSegment(sketch, "E40.3", {"start": v(38.1, 38.1) * mm, "end": v(368.3, 38.1) * mm, "construction": true});
            skCircle(sketch, "E41.0.0.8", {"center": v(38.1, 220.98) * mm, "radius": 1.59 * mm, "construction": true});
            skCircle(sketch, "E41.0.0.9", {"center": v(38.1, 243.84) * mm, "radius": 1.59 * mm, "construction": true});
            skCircle(sketch, "E42.0.1.0", {"center": v(60.96, 38.1) * mm, "radius": 1.59 * mm, "construction": true});
            skCircle(sketch, "E42.0.1.1", {"center": v(60.96, 60.96) * mm, "radius": 1.59 * mm, "construction": true});
            skCircle(sketch, "E42.0.1.2", {"center": v(60.96, 83.82) * mm, "radius": 1.59 * mm, "construction": true});
            skCircle(sketch, "E42.0.1.3", {"center": v(60.96, 106.68) * mm, "radius": 1.59 * mm, "construction": true});
            skCircle(sketch, "E42.0.1.4", {"center": v(60.96, 129.54) * mm, "radius": 1.59 * mm, "construction": true});
            skCircle(sketch, "E42.0.1.5", {"center": v(60.96, 152.4) * mm, "radius": 1.59 * mm, "construction": true});
            skCircle(sketch, "E42.0.1.6", {"center": v(60.96, 175.26) * mm, "radius": 1.59 * mm, "construction": true});
            skCircle(sketch, "E42.0.1.7", {"center": v(60.96, 198.12) * mm, "radius": 1.59 * mm, "construction": true});
            skCircle(sketch, "E42.0.1.8", {"center": v(60.96, 220.98) * mm, "radius": 1.59 * mm, "construction": true});
            skCircle(sketch, "E42.0.1.9", {"center": v(60.96, 243.84) * mm, "radius": 1.59 * mm, "construction": true});
            skCircle(sketch, "E42.0.2.0", {"center": v(83.82, 38.1) * mm, "radius": 1.59 * mm, "construction": true});
            skCircle(sketch, "E42.0.2.1", {"center": v(83.82, 60.96) * mm, "radius": 1.59 * mm, "construction": true});
            skCircle(sketch, "E42.0.2.2", {"center": v(83.82, 83.82) * mm, "radius": 1.59 * mm, "construction": true});
            skCircle(sketch, "E42.0.2.3", {"center": v(83.82, 106.68) * mm, "radius": 1.59 * mm, "construction": true});
            skCircle(sketch, "E42.0.2.4", {"center": v(83.82, 129.54) * mm, "radius": 1.59 * mm, "construction": true});
            skCircle(sketch, "E42.0.2.5", {"center": v(83.82, 152.4) * mm, "radius": 1.59 * mm, "construction": true});
            skCircle(sketch, "E42.0.2.6", {"center": v(83.82, 175.26) * mm, "radius": 1.59 * mm, "construction": true});
            skCircle(sketch, "E42.0.2.7", {"center": v(83.82, 198.12) * mm, "radius": 1.59 * mm, "construction": true});
            skCircle(sketch, "E42.0.2.8", {"center": v(83.82, 220.98) * mm, "radius": 1.59 * mm, "construction": true});
            skCircle(sketch, "E42.0.2.9", {"center": v(83.82, 243.84) * mm, "radius": 1.59 * mm, "construction": true});
            skCircle(sketch, "E43.0.0.10", {"center": v(38.1, 266.7) * mm, "radius": 1.59 * mm, "construction": true});
            skCircle(sketch, "E43.0.1.10", {"center": v(60.96, 266.7) * mm, "radius": 1.59 * mm, "construction": true});
            skCircle(sketch, "E43.0.2.10", {"center": v(83.82, 266.7) * mm, "radius": 1.59 * mm, "construction": true});
            skCircle(sketch, "E44", {"center": v(121.92, 38.1) * mm, "radius": 3.18 * mm, "construction": true});
            skCircle(sketch, "E45.0.1.0", {"center": v(121.92, 63.5) * mm, "radius": 3.18 * mm, "construction": true});
            skCircle(sketch, "E45.0.2.0", {"center": v(121.92, 88.9) * mm, "radius": 3.18 * mm, "construction": true});
            skCircle(sketch, "E45.0.3.0", {"center": v(121.92, 114.3) * mm, "radius": 3.18 * mm, "construction": true});
            skCircle(sketch, "E45.0.4.0", {"center": v(121.92, 139.7) * mm, "radius": 3.18 * mm, "construction": true});
            skCircle(sketch, "E45.0.5.0", {"center": v(121.92, 165.1) * mm, "radius": 3.18 * mm, "construction": true});
            skCircle(sketch, "E45.0.6.0", {"center": v(121.92, 190.5) * mm, "radius": 3.18 * mm, "construction": true});
            skCircle(sketch, "E45.0.7.0", {"center": v(121.92, 215.9) * mm, "radius": 3.18 * mm, "construction": true});
            skCircle(sketch, "E45.0.8.0", {"center": v(121.92, 241.3) * mm, "radius": 3.18 * mm, "construction": true});
            skCircle(sketch, "E45.0.9.0", {"center": v(121.92, 266.7) * mm, "radius": 3.18 * mm, "construction": true});
            skCircle(sketch, "E45.1.0.0", {"center": v(147.32, 38.1) * mm, "radius": 3.18 * mm, "construction": true});
            skCircle(sketch, "E45.1.1.0", {"center": v(147.32, 63.5) * mm, "radius": 3.18 * mm, "construction": true});
            skCircle(sketch, "E45.1.2.0", {"center": v(147.32, 88.9) * mm, "radius": 3.18 * mm, "construction": true});
            skCircle(sketch, "E45.1.3.0", {"center": v(147.32, 114.3) * mm, "radius": 3.18 * mm, "construction": true});
            skCircle(sketch, "E45.1.4.0", {"center": v(147.32, 139.7) * mm, "radius": 3.18 * mm, "construction": true});
            skCircle(sketch, "E45.1.5.0", {"center": v(147.32, 165.1) * mm, "radius": 3.18 * mm, "construction": true});
            skCircle(sketch, "E45.1.6.0", {"center": v(147.32, 190.5) * mm, "radius": 3.18 * mm, "construction": true});
            skCircle(sketch, "E45.1.7.0", {"center": v(147.32, 215.9) * mm, "radius": 3.18 * mm, "construction": true});
            skCircle(sketch, "E45.1.8.0", {"center": v(147.32, 241.3) * mm, "radius": 3.18 * mm, "construction": true});
            skCircle(sketch, "E45.1.9.0", {"center": v(147.32, 266.7) * mm, "radius": 3.18 * mm, "construction": true});
            skCircle(sketch, "E45.2.0.0", {"center": v(172.72, 38.1) * mm, "radius": 3.18 * mm, "construction": true});
            skCircle(sketch, "E45.2.1.0", {"center": v(172.72, 63.5) * mm, "radius": 3.18 * mm, "construction": true});
            skCircle(sketch, "E45.2.2.0", {"center": v(172.72, 88.9) * mm, "radius": 3.18 * mm, "construction": true});
            skCircle(sketch, "E45.2.3.0", {"center": v(172.72, 114.3) * mm, "radius": 3.18 * mm, "construction": true});
            skCircle(sketch, "E45.2.4.0", {"center": v(172.72, 139.7) * mm, "radius": 3.18 * mm, "construction": true});
            skCircle(sketch, "E45.2.5.0", {"center": v(172.72, 165.1) * mm, "radius": 3.18 * mm, "construction": true});
            skCircle(sketch, "E45.2.6.0", {"center": v(172.72, 190.5) * mm, "radius": 3.18 * mm, "construction": true});
            skCircle(sketch, "E45.2.7.0", {"center": v(172.72, 215.9) * mm, "radius": 3.18 * mm, "construction": true});
            skCircle(sketch, "E45.2.8.0", {"center": v(172.72, 241.3) * mm, "radius": 3.18 * mm, "construction": true});
            skCircle(sketch, "E45.2.9.0", {"center": v(172.72, 266.7) * mm, "radius": 3.18 * mm, "construction": true});
            skLineSegment(sketch, "E45.direction1", {"start": v(121.92, 38.1) * mm, "end": v(147.32, 38.1) * mm, "construction": true});
            skLineSegment(sketch, "E45.direction2", {"start": v(121.92, 38.1) * mm, "end": v(121.92, 63.5) * mm, "construction": true});
            skCircle(sketch, "E46", {"center": v(217.17, 38.1) * mm, "radius": 6.35 * mm, "construction": true});
            skCircle(sketch, "E47.0.1.0", {"center": v(217.17, 66.67) * mm, "radius": 6.35 * mm, "construction": true});
            skCircle(sketch, "E47.0.2.0", {"center": v(217.17, 95.25) * mm, "radius": 6.35 * mm, "construction": true});
            skCircle(sketch, "E47.0.3.0", {"center": v(217.17, 123.82) * mm, "radius": 6.35 * mm, "construction": true});
            skCircle(sketch, "E47.0.4.0", {"center": v(217.17, 152.4) * mm, "radius": 6.35 * mm, "construction": true});
            skCircle(sketch, "E47.0.5.0", {"center": v(217.17, 180.97) * mm, "radius": 6.35 * mm, "construction": true});
            skCircle(sketch, "E47.0.6.0", {"center": v(217.17, 209.55) * mm, "radius": 6.35 * mm, "construction": true});
            skCircle(sketch, "E47.0.7.0", {"center": v(217.17, 238.13) * mm, "radius": 6.35 * mm, "construction": true});
            skCircle(sketch, "E47.0.8.0", {"center": v(217.17, 266.7) * mm, "radius": 6.35 * mm, "construction": true});
            skCircle(sketch, "E47.1.0.0", {"center": v(245.75, 38.1) * mm, "radius": 6.35 * mm, "construction": true});
            skCircle(sketch, "E47.1.1.0", {"center": v(245.75, 66.67) * mm, "radius": 6.35 * mm, "construction": true});
            skCircle(sketch, "E47.1.2.0", {"center": v(245.75, 95.25) * mm, "radius": 6.35 * mm, "construction": true});
            skCircle(sketch, "E47.1.3.0", {"center": v(245.75, 123.82) * mm, "radius": 6.35 * mm, "construction": true});
            skCircle(sketch, "E47.1.4.0", {"center": v(245.75, 152.4) * mm, "radius": 6.35 * mm, "construction": true});
            skCircle(sketch, "E47.1.5.0", {"center": v(245.75, 180.97) * mm, "radius": 6.35 * mm, "construction": true});
            skCircle(sketch, "E47.1.6.0", {"center": v(245.75, 209.55) * mm, "radius": 6.35 * mm, "construction": true});
            skCircle(sketch, "E47.1.7.0", {"center": v(245.75, 238.13) * mm, "radius": 6.35 * mm, "construction": true});
            skCircle(sketch, "E47.1.8.0", {"center": v(245.75, 266.7) * mm, "radius": 6.35 * mm, "construction": true});
            skCircle(sketch, "E47.2.0.0", {"center": v(274.32, 38.1) * mm, "radius": 6.35 * mm, "construction": true});
            skCircle(sketch, "E47.2.1.0", {"center": v(274.32, 66.67) * mm, "radius": 6.35 * mm, "construction": true});
            skCircle(sketch, "E47.2.2.0", {"center": v(274.32, 95.25) * mm, "radius": 6.35 * mm, "construction": true});
            skCircle(sketch, "E47.2.3.0", {"center": v(274.32, 123.82) * mm, "radius": 6.35 * mm, "construction": true});
            skCircle(sketch, "E47.2.4.0", {"center": v(274.32, 152.4) * mm, "radius": 6.35 * mm, "construction": true});
            skCircle(sketch, "E47.2.5.0", {"center": v(274.32, 180.97) * mm, "radius": 6.35 * mm, "construction": true});
            skCircle(sketch, "E47.2.6.0", {"center": v(274.32, 209.55) * mm, "radius": 6.35 * mm, "construction": true});
            skCircle(sketch, "E47.2.7.0", {"center": v(274.32, 238.13) * mm, "radius": 6.35 * mm, "construction": true});
            skCircle(sketch, "E47.2.8.0", {"center": v(274.32, 266.7) * mm, "radius": 6.35 * mm, "construction": true});
            skLineSegment(sketch, "E47.direction1", {"start": v(217.17, 38.1) * mm, "end": v(245.75, 38.1) * mm, "construction": true});
            skLineSegment(sketch, "E47.direction2", {"start": v(217.17, 38.1) * mm, "end": v(217.17, 66.67) * mm, "construction": true});
            skCircle(sketch, "E48", {"center": v(325.12, 38.1) * mm, "radius": 9.53 * mm, "construction": true});
            skCircle(sketch, "E49.0.1.0", {"center": v(325.12, 70.76) * mm, "radius": 9.53 * mm, "construction": true});
            skCircle(sketch, "E49.0.2.0", {"center": v(325.12, 103.41) * mm, "radius": 9.53 * mm, "construction": true});
            skCircle(sketch, "E49.0.3.0", {"center": v(325.12, 136.07) * mm, "radius": 9.53 * mm, "construction": true});
            skCircle(sketch, "E49.0.4.0", {"center": v(325.12, 168.73) * mm, "radius": 9.53 * mm, "construction": true});
            skCircle(sketch, "E49.0.5.0", {"center": v(325.12, 201.39) * mm, "radius": 9.53 * mm, "construction": true});
            skCircle(sketch, "E49.0.6.0", {"center": v(325.12, 234.04) * mm, "radius": 9.53 * mm, "construction": true});
            skCircle(sketch, "E49.0.7.0", {"center": v(325.12, 266.7) * mm, "radius": 9.53 * mm, "construction": true});
            skCircle(sketch, "E49.1.0.0", {"center": v(357.78, 38.1) * mm, "radius": 9.53 * mm, "construction": true});
            skCircle(sketch, "E49.1.1.0", {"center": v(357.78, 70.76) * mm, "radius": 9.53 * mm, "construction": true});
            skCircle(sketch, "E49.1.2.0", {"center": v(357.78, 103.41) * mm, "radius": 9.53 * mm, "construction": true});
            skCircle(sketch, "E49.1.3.0", {"center": v(357.78, 136.07) * mm, "radius": 9.53 * mm, "construction": true});
            skCircle(sketch, "E49.1.4.0", {"center": v(357.78, 168.73) * mm, "radius": 9.53 * mm, "construction": true});
            skCircle(sketch, "E49.1.5.0", {"center": v(357.78, 201.39) * mm, "radius": 9.53 * mm, "construction": true});
            skCircle(sketch, "E49.1.6.0", {"center": v(357.78, 234.04) * mm, "radius": 9.53 * mm, "construction": true});
            skCircle(sketch, "E49.1.7.0", {"center": v(357.78, 266.7) * mm, "radius": 9.53 * mm, "construction": true});
            skLineSegment(sketch, "E49.direction1", {"start": v(325.12, 38.1) * mm, "end": v(357.78, 38.1) * mm, "construction": true});
            skLineSegment(sketch, "E49.direction2", {"start": v(325.12, 38.1) * mm, "end": v(325.12, 70.76) * mm, "construction": true});
            skPoint(sketch, "E50.visualSharp", {"position": v(0, 304.8) * mm});
            skArc(sketch, "E50.filletArc", {"start": v(50.8, 304.8) * mm, "mid": v(14.88, 289.92) * mm, "end": v(0, 254) * mm});
            skPoint(sketch, "E51.visualSharp", {"position": v(406.4, 304.8) * mm});
            skArc(sketch, "E51.filletArc", {"start": v(406.4, 254) * mm, "mid": v(391.52, 289.92) * mm, "end": v(355.6, 304.8) * mm});
            skPoint(sketch, "E52.visualSharp", {"position": v(406.4, 0) * mm});
            skArc(sketch, "E52.filletArc", {"start": v(355.6, 0) * mm, "mid": v(391.52, 14.88) * mm, "end": v(406.4, 50.8) * mm});
            skPoint(sketch, "E53.visualSharp", {"position": v(0, 0) * mm});
            skLineSegment(sketch, "E54", {"start": v(12.7, 163.83) * mm, "end": v(90.17, 163.83) * mm});
            skLineSegment(sketch, "E55", {"start": v(102.87, 151.13) * mm, "end": v(102.87, 139.7) * mm});
            skLineSegment(sketch, "E56", {"start": v(115.57, 127) * mm, "end": v(182.25, 127) * mm});
            skLineSegment(sketch, "E57", {"start": v(194.95, 114.3) * mm, "end": v(194.95, 93.66) * mm});
            skLineSegment(sketch, "E58", {"start": v(207.65, 80.96) * mm, "end": v(287.02, 80.96) * mm});
            skLineSegment(sketch, "E59", {"start": v(299.72, 68.26) * mm, "end": v(299.72, 12.7) * mm});
            skLineSegment(sketch, "E60", {"start": v(83.82, 152.4) * mm, "end": v(102.87, 152.4) * mm, "construction": true});
            skLineSegment(sketch, "E61", {"start": v(102.87, 152.4) * mm, "end": v(121.92, 152.4) * mm, "construction": true});
            skLineSegment(sketch, "E62", {"start": v(172.72, 114.3) * mm, "end": v(194.95, 114.3) * mm, "construction": true});
            skLineSegment(sketch, "E63", {"start": v(194.95, 114.3) * mm, "end": v(217.17, 114.3) * mm, "construction": true});
            skLineSegment(sketch, "E64", {"start": v(274.32, 66.67) * mm, "end": v(299.72, 66.67) * mm, "construction": true});
            skLineSegment(sketch, "E65", {"start": v(299.72, 66.67) * mm, "end": v(325.12, 66.67) * mm, "construction": true});
            skLineSegment(sketch, "E66", {"start": v(60.96, 175.26) * mm, "end": v(60.96, 163.83) * mm, "construction": true});
            skLineSegment(sketch, "E67", {"start": v(60.96, 163.83) * mm, "end": v(60.96, 152.4) * mm, "construction": true});
            skLineSegment(sketch, "E68", {"start": v(147.32, 127) * mm, "end": v(147.32, 114.3) * mm, "construction": true});
            skLineSegment(sketch, "E69", {"start": v(147.32, 139.7) * mm, "end": v(147.32, 127) * mm, "construction": true});
            skLineSegment(sketch, "E70", {"start": v(245.75, 66.67) * mm, "end": v(245.75, 80.96) * mm, "construction": true});
            skLineSegment(sketch, "E71", {"start": v(245.75, 80.96) * mm, "end": v(245.75, 95.25) * mm, "construction": true});
            skArc(sketch, "E72.filletArc", {"start": v(299.72, 12.7) * mm, "mid": v(303.44, 3.72) * mm, "end": v(312.42, 0) * mm});
            skPoint(sketch, "E73.visualSharp", {"position": v(299.72, 80.96) * mm});
            skArc(sketch, "E73.filletArc", {"start": v(299.72, 68.26) * mm, "mid": v(296, 77.24) * mm, "end": v(287.02, 80.96) * mm});
            skPoint(sketch, "E74.visualSharp", {"position": v(194.95, 80.96) * mm});
            skArc(sketch, "E74.filletArc", {"start": v(194.95, 93.66) * mm, "mid": v(198.66, 84.68) * mm, "end": v(207.65, 80.96) * mm});
            skPoint(sketch, "E75.visualSharp", {"position": v(194.95, 127) * mm});
            skArc(sketch, "E75.filletArc", {"start": v(194.95, 114.3) * mm, "mid": v(191.23, 123.28) * mm, "end": v(182.25, 127) * mm});
            skPoint(sketch, "E76.visualSharp", {"position": v(102.87, 127) * mm});
            skArc(sketch, "E76.filletArc", {"start": v(102.87, 139.7) * mm, "mid": v(106.59, 130.72) * mm, "end": v(115.57, 127) * mm});
            skPoint(sketch, "E77.visualSharp", {"position": v(102.87, 163.83) * mm});
            skArc(sketch, "E77.filletArc", {"start": v(102.87, 151.13) * mm, "mid": v(99.15, 160.11) * mm, "end": v(90.17, 163.83) * mm});
            skArc(sketch, "E78.filletArc", {"start": v(0, 176.53) * mm, "mid": v(3.72, 167.55) * mm, "end": v(12.7, 163.83) * mm});
            skCircle(sketch, "E79", {"center": v(102.87, 176.53) * mm, "radius": 1.65 * mm});
            skCircle(sketch, "E80", {"center": v(194.95, 139.7) * mm, "radius": 1.65 * mm});
            skCircle(sketch, "E81", {"center": v(299.72, 93.66) * mm, "radius": 1.65 * mm});
            skCircle(sketch, "E82.0", {"center": v(19.05, 50.8) * mm, "radius": 1.65 * mm, "construction": true});
            skLineSegment(sketch, "E83", {"start": v(102.87, 163.83) * mm, "end": v(102.87, 176.53) * mm, "construction": true});
            skLineSegment(sketch, "E84", {"start": v(194.95, 127) * mm, "end": v(194.95, 139.7) * mm, "construction": true});
            skLineSegment(sketch, "E85", {"start": v(299.72, 93.66) * mm, "end": v(299.72, 80.96) * mm, "construction": true});
            skCircle(sketch, "E86", {"center": v(19.05, 182.88) * mm, "radius": 1.65 * mm});
            skLineSegment(sketch, "E87", {"start": v(19.05, 163.83) * mm, "end": v(19.05, 182.88) * mm, "construction": true});
            skLineSegment(sketch, "E88", {"start": v(19.05, 182.88) * mm, "end": v(0, 182.88) * mm, "construction": true});
            skCircle(sketch, "E89.0", {"center": v(355.6, 19.05) * mm, "radius": 1.65 * mm, "construction": true});
            skCircle(sketch, "E90", {"center": v(318.77, 19.05) * mm, "radius": 1.65 * mm});
            skLineSegment(sketch, "E91", {"start": v(299.72, 19.05) * mm, "end": v(318.77, 19.05) * mm, "construction": true});
            skLineSegment(sketch, "E92", {"start": v(318.77, 0) * mm, "end": v(318.77, 19.05) * mm, "construction": true});
            skSolve(sketch);
        }
        {
            var Q0;
            Q0=qCreatedBy(makeId("Top.planeOp"),FACE);
            var sketch = newSketch(context, id + "F6", { "sketchPlane" : qUnion([Q0])});
            skCircle(sketch, "E93", {"center": v(38.1, 38.1) * mm, "radius": 1.59 * mm, "construction": true});
            skCircle(sketch, "E94.0.1.0", {"center": v(38.1, 60.96) * mm, "radius": 1.59 * mm, "construction": true});
            skCircle(sketch, "E94.0.2.0", {"center": v(38.1, 83.82) * mm, "radius": 1.59 * mm, "construction": true});
            skCircle(sketch, "E94.0.3.0", {"center": v(38.1, 106.68) * mm, "radius": 1.59 * mm, "construction": true});
            skCircle(sketch, "E94.0.4.0", {"center": v(38.1, 129.54) * mm, "radius": 1.59 * mm, "construction": true});
            skCircle(sketch, "E94.0.5.0", {"center": v(38.1, 152.4) * mm, "radius": 1.59 * mm, "construction": true});
            skCircle(sketch, "E94.0.6.0", {"center": v(38.1, 175.26) * mm, "radius": 1.59 * mm, "construction": true});
            skCircle(sketch, "E94.0.7.0", {"center": v(38.1, 198.12) * mm, "radius": 1.59 * mm, "construction": true});
            skLineSegment(sketch, "E94.direction1", {"start": v(38.1, 38.1) * mm, "end": v(60.96, 38.1) * mm, "construction": true});
            skLineSegment(sketch, "E94.direction2", {"start": v(38.1, 38.1) * mm, "end": v(38.1, 60.96) * mm, "construction": true});
            skLineSegment(sketch, "E95.bottom", {"start": v(115.57, 304.8) * mm, "end": v(355.6, 304.8) * mm});
            skLineSegment(sketch, "E95.top", {"start": v(0, 0) * mm, "end": v(406.4, 0) * mm, "construction": true});
            skLineSegment(sketch, "E95.left", {"start": v(0, 304.8) * mm, "end": v(0, 0) * mm, "construction": true});
            skLineSegment(sketch, "E95.right", {"start": v(406.4, 254) * mm, "end": v(406.4, 132.44) * mm});
            skLineSegment(sketch, "E96.0", {"start": v(38.1, 266.7) * mm, "end": v(38.1, 38.1) * mm, "construction": true});
            skLineSegment(sketch, "E96.1", {"start": v(38.1, 266.7) * mm, "end": v(368.3, 266.7) * mm, "construction": true});
            skLineSegment(sketch, "E96.2", {"start": v(368.3, 266.7) * mm, "end": v(368.3, 38.1) * mm, "construction": true});
            skLineSegment(sketch, "E96.3", {"start": v(38.1, 38.1) * mm, "end": v(368.3, 38.1) * mm, "construction": true});
            skCircle(sketch, "E97.0.0.8", {"center": v(38.1, 220.98) * mm, "radius": 1.59 * mm, "construction": true});
            skCircle(sketch, "E97.0.0.9", {"center": v(38.1, 243.84) * mm, "radius": 1.59 * mm, "construction": true});
            skCircle(sketch, "E98.0.1.0", {"center": v(60.96, 38.1) * mm, "radius": 1.59 * mm, "construction": true});
            skCircle(sketch, "E98.0.1.1", {"center": v(60.96, 60.96) * mm, "radius": 1.59 * mm, "construction": true});
            skCircle(sketch, "E98.0.1.2", {"center": v(60.96, 83.82) * mm, "radius": 1.59 * mm, "construction": true});
            skCircle(sketch, "E98.0.1.3", {"center": v(60.96, 106.68) * mm, "radius": 1.59 * mm, "construction": true});
            skCircle(sketch, "E98.0.1.4", {"center": v(60.96, 129.54) * mm, "radius": 1.59 * mm, "construction": true});
            skCircle(sketch, "E98.0.1.5", {"center": v(60.96, 152.4) * mm, "radius": 1.59 * mm, "construction": true});
            skCircle(sketch, "E98.0.1.6", {"center": v(60.96, 175.26) * mm, "radius": 1.59 * mm, "construction": true});
            skCircle(sketch, "E98.0.1.7", {"center": v(60.96, 198.12) * mm, "radius": 1.59 * mm, "construction": true});
            skCircle(sketch, "E98.0.1.8", {"center": v(60.96, 220.98) * mm, "radius": 1.59 * mm, "construction": true});
            skCircle(sketch, "E98.0.1.9", {"center": v(60.96, 243.84) * mm, "radius": 1.59 * mm, "construction": true});
            skCircle(sketch, "E98.0.2.0", {"center": v(83.82, 38.1) * mm, "radius": 1.59 * mm, "construction": true});
            skCircle(sketch, "E98.0.2.1", {"center": v(83.82, 60.96) * mm, "radius": 1.59 * mm, "construction": true});
            skCircle(sketch, "E98.0.2.2", {"center": v(83.82, 83.82) * mm, "radius": 1.59 * mm, "construction": true});
            skCircle(sketch, "E98.0.2.3", {"center": v(83.82, 106.68) * mm, "radius": 1.59 * mm, "construction": true});
            skCircle(sketch, "E98.0.2.4", {"center": v(83.82, 129.54) * mm, "radius": 1.59 * mm, "construction": true});
            skCircle(sketch, "E98.0.2.5", {"center": v(83.82, 152.4) * mm, "radius": 1.59 * mm, "construction": true});
            skCircle(sketch, "E98.0.2.6", {"center": v(83.82, 175.26) * mm, "radius": 1.59 * mm, "construction": true});
            skCircle(sketch, "E98.0.2.7", {"center": v(83.82, 198.12) * mm, "radius": 1.59 * mm, "construction": true});
            skCircle(sketch, "E98.0.2.8", {"center": v(83.82, 220.98) * mm, "radius": 1.59 * mm, "construction": true});
            skCircle(sketch, "E98.0.2.9", {"center": v(83.82, 243.84) * mm, "radius": 1.59 * mm, "construction": true});
            skCircle(sketch, "E99.0.0.10", {"center": v(38.1, 266.7) * mm, "radius": 1.59 * mm, "construction": true});
            skCircle(sketch, "E99.0.1.10", {"center": v(60.96, 266.7) * mm, "radius": 1.59 * mm, "construction": true});
            skCircle(sketch, "E99.0.2.10", {"center": v(83.82, 266.7) * mm, "radius": 1.59 * mm, "construction": true});
            skCircle(sketch, "E100", {"center": v(121.92, 38.1) * mm, "radius": 3.18 * mm, "construction": true});
            skCircle(sketch, "E101.0.1.0", {"center": v(121.92, 63.5) * mm, "radius": 3.18 * mm, "construction": true});
            skCircle(sketch, "E101.0.2.0", {"center": v(121.92, 88.9) * mm, "radius": 3.18 * mm, "construction": true});
            skCircle(sketch, "E101.0.3.0", {"center": v(121.92, 114.3) * mm, "radius": 3.18 * mm, "construction": true});
            skCircle(sketch, "E101.0.4.0", {"center": v(121.92, 139.7) * mm, "radius": 3.18 * mm, "construction": true});
            skCircle(sketch, "E101.0.5.0", {"center": v(121.92, 165.1) * mm, "radius": 3.18 * mm, "construction": true});
            skCircle(sketch, "E101.0.6.0", {"center": v(121.92, 190.5) * mm, "radius": 3.18 * mm, "construction": true});
            skCircle(sketch, "E101.0.7.0", {"center": v(121.92, 215.9) * mm, "radius": 3.18 * mm, "construction": true});
            skCircle(sketch, "E101.0.8.0", {"center": v(121.92, 241.3) * mm, "radius": 3.18 * mm, "construction": true});
            skCircle(sketch, "E101.0.9.0", {"center": v(121.92, 266.7) * mm, "radius": 3.18 * mm, "construction": true});
            skCircle(sketch, "E101.1.0.0", {"center": v(147.32, 38.1) * mm, "radius": 3.18 * mm, "construction": true});
            skCircle(sketch, "E101.1.1.0", {"center": v(147.32, 63.5) * mm, "radius": 3.18 * mm, "construction": true});
            skCircle(sketch, "E101.1.2.0", {"center": v(147.32, 88.9) * mm, "radius": 3.18 * mm, "construction": true});
            skCircle(sketch, "E101.1.3.0", {"center": v(147.32, 114.3) * mm, "radius": 3.18 * mm, "construction": true});
            skCircle(sketch, "E101.1.4.0", {"center": v(147.32, 139.7) * mm, "radius": 3.18 * mm, "construction": true});
            skCircle(sketch, "E101.1.5.0", {"center": v(147.32, 165.1) * mm, "radius": 3.18 * mm, "construction": true});
            skCircle(sketch, "E101.1.6.0", {"center": v(147.32, 190.5) * mm, "radius": 3.18 * mm, "construction": true});
            skCircle(sketch, "E101.1.7.0", {"center": v(147.32, 215.9) * mm, "radius": 3.18 * mm, "construction": true});
            skCircle(sketch, "E101.1.8.0", {"center": v(147.32, 241.3) * mm, "radius": 3.18 * mm, "construction": true});
            skCircle(sketch, "E101.1.9.0", {"center": v(147.32, 266.7) * mm, "radius": 3.18 * mm, "construction": true});
            skCircle(sketch, "E101.2.0.0", {"center": v(172.72, 38.1) * mm, "radius": 3.18 * mm, "construction": true});
            skCircle(sketch, "E101.2.1.0", {"center": v(172.72, 63.5) * mm, "radius": 3.18 * mm, "construction": true});
            skCircle(sketch, "E101.2.2.0", {"center": v(172.72, 88.9) * mm, "radius": 3.18 * mm, "construction": true});
            skCircle(sketch, "E101.2.3.0", {"center": v(172.72, 114.3) * mm, "radius": 3.18 * mm, "construction": true});
            skCircle(sketch, "E101.2.4.0", {"center": v(172.72, 139.7) * mm, "radius": 3.18 * mm, "construction": true});
            skCircle(sketch, "E101.2.5.0", {"center": v(172.72, 165.1) * mm, "radius": 3.18 * mm, "construction": true});
            skCircle(sketch, "E101.2.6.0", {"center": v(172.72, 190.5) * mm, "radius": 3.18 * mm, "construction": true});
            skCircle(sketch, "E101.2.7.0", {"center": v(172.72, 215.9) * mm, "radius": 3.18 * mm, "construction": true});
            skCircle(sketch, "E101.2.8.0", {"center": v(172.72, 241.3) * mm, "radius": 3.18 * mm, "construction": true});
            skCircle(sketch, "E101.2.9.0", {"center": v(172.72, 266.7) * mm, "radius": 3.18 * mm, "construction": true});
            skLineSegment(sketch, "E101.direction1", {"start": v(121.92, 38.1) * mm, "end": v(147.32, 38.1) * mm, "construction": true});
            skLineSegment(sketch, "E101.direction2", {"start": v(121.92, 38.1) * mm, "end": v(121.92, 63.5) * mm, "construction": true});
            skCircle(sketch, "E102", {"center": v(217.17, 38.1) * mm, "radius": 6.35 * mm, "construction": true});
            skCircle(sketch, "E103.0.1.0", {"center": v(217.17, 66.67) * mm, "radius": 6.35 * mm, "construction": true});
            skCircle(sketch, "E103.0.2.0", {"center": v(217.17, 95.25) * mm, "radius": 6.35 * mm, "construction": true});
            skCircle(sketch, "E103.0.3.0", {"center": v(217.17, 123.82) * mm, "radius": 6.35 * mm, "construction": true});
            skCircle(sketch, "E103.0.4.0", {"center": v(217.17, 152.4) * mm, "radius": 6.35 * mm, "construction": true});
            skCircle(sketch, "E103.0.5.0", {"center": v(217.17, 180.97) * mm, "radius": 6.35 * mm, "construction": true});
            skCircle(sketch, "E103.0.6.0", {"center": v(217.17, 209.55) * mm, "radius": 6.35 * mm, "construction": true});
            skCircle(sketch, "E103.0.7.0", {"center": v(217.17, 238.12) * mm, "radius": 6.35 * mm, "construction": true});
            skCircle(sketch, "E103.0.8.0", {"center": v(217.17, 266.7) * mm, "radius": 6.35 * mm, "construction": true});
            skCircle(sketch, "E103.1.0.0", {"center": v(245.74, 38.1) * mm, "radius": 6.35 * mm, "construction": true});
            skCircle(sketch, "E103.1.1.0", {"center": v(245.74, 66.67) * mm, "radius": 6.35 * mm, "construction": true});
            skCircle(sketch, "E103.1.2.0", {"center": v(245.74, 95.25) * mm, "radius": 6.35 * mm, "construction": true});
            skCircle(sketch, "E103.1.3.0", {"center": v(245.74, 123.82) * mm, "radius": 6.35 * mm, "construction": true});
            skCircle(sketch, "E103.1.4.0", {"center": v(245.74, 152.4) * mm, "radius": 6.35 * mm, "construction": true});
            skCircle(sketch, "E103.1.5.0", {"center": v(245.74, 180.97) * mm, "radius": 6.35 * mm, "construction": true});
            skCircle(sketch, "E103.1.6.0", {"center": v(245.74, 209.55) * mm, "radius": 6.35 * mm, "construction": true});
            skCircle(sketch, "E103.1.7.0", {"center": v(245.74, 238.12) * mm, "radius": 6.35 * mm, "construction": true});
            skCircle(sketch, "E103.1.8.0", {"center": v(245.74, 266.7) * mm, "radius": 6.35 * mm, "construction": true});
            skCircle(sketch, "E103.2.0.0", {"center": v(274.32, 38.1) * mm, "radius": 6.35 * mm, "construction": true});
            skCircle(sketch, "E103.2.1.0", {"center": v(274.32, 66.67) * mm, "radius": 6.35 * mm, "construction": true});
            skCircle(sketch, "E103.2.2.0", {"center": v(274.32, 95.25) * mm, "radius": 6.35 * mm, "construction": true});
            skCircle(sketch, "E103.2.3.0", {"center": v(274.32, 123.82) * mm, "radius": 6.35 * mm, "construction": true});
            skCircle(sketch, "E103.2.4.0", {"center": v(274.32, 152.4) * mm, "radius": 6.35 * mm, "construction": true});
            skCircle(sketch, "E103.2.5.0", {"center": v(274.32, 180.97) * mm, "radius": 6.35 * mm, "construction": true});
            skCircle(sketch, "E103.2.6.0", {"center": v(274.32, 209.55) * mm, "radius": 6.35 * mm, "construction": true});
            skCircle(sketch, "E103.2.7.0", {"center": v(274.32, 238.12) * mm, "radius": 6.35 * mm, "construction": true});
            skCircle(sketch, "E103.2.8.0", {"center": v(274.32, 266.7) * mm, "radius": 6.35 * mm, "construction": true});
            skLineSegment(sketch, "E103.direction1", {"start": v(217.17, 38.1) * mm, "end": v(245.74, 38.1) * mm, "construction": true});
            skLineSegment(sketch, "E103.direction2", {"start": v(217.17, 38.1) * mm, "end": v(217.17, 66.67) * mm, "construction": true});
            skCircle(sketch, "E104", {"center": v(325.12, 38.1) * mm, "radius": 9.53 * mm, "construction": true});
            skCircle(sketch, "E105.0.1.0", {"center": v(325.12, 70.76) * mm, "radius": 9.53 * mm, "construction": true});
            skCircle(sketch, "E105.0.2.0", {"center": v(325.12, 103.41) * mm, "radius": 9.53 * mm, "construction": true});
            skCircle(sketch, "E105.0.3.0", {"center": v(325.12, 136.07) * mm, "radius": 9.53 * mm, "construction": true});
            skCircle(sketch, "E105.0.4.0", {"center": v(325.12, 168.73) * mm, "radius": 9.53 * mm, "construction": true});
            skCircle(sketch, "E105.0.5.0", {"center": v(325.12, 201.39) * mm, "radius": 9.53 * mm, "construction": true});
            skCircle(sketch, "E105.0.6.0", {"center": v(325.12, 234.04) * mm, "radius": 9.53 * mm, "construction": true});
            skCircle(sketch, "E105.0.7.0", {"center": v(325.12, 266.7) * mm, "radius": 9.53 * mm, "construction": true});
            skCircle(sketch, "E105.1.0.0", {"center": v(357.78, 38.1) * mm, "radius": 9.53 * mm, "construction": true});
            skCircle(sketch, "E105.1.1.0", {"center": v(357.78, 70.76) * mm, "radius": 9.53 * mm, "construction": true});
            skCircle(sketch, "E105.1.2.0", {"center": v(357.78, 103.41) * mm, "radius": 9.53 * mm, "construction": true});
            skCircle(sketch, "E105.1.3.0", {"center": v(357.78, 136.07) * mm, "radius": 9.53 * mm, "construction": true});
            skCircle(sketch, "E105.1.4.0", {"center": v(357.78, 168.73) * mm, "radius": 9.53 * mm, "construction": true});
            skCircle(sketch, "E105.1.5.0", {"center": v(357.78, 201.39) * mm, "radius": 9.53 * mm, "construction": true});
            skCircle(sketch, "E105.1.6.0", {"center": v(357.78, 234.04) * mm, "radius": 9.53 * mm, "construction": true});
            skCircle(sketch, "E105.1.7.0", {"center": v(357.78, 266.7) * mm, "radius": 9.53 * mm, "construction": true});
            skLineSegment(sketch, "E105.direction1", {"start": v(325.12, 38.1) * mm, "end": v(357.78, 38.1) * mm, "construction": true});
            skLineSegment(sketch, "E105.direction2", {"start": v(325.12, 38.1) * mm, "end": v(325.12, 70.76) * mm, "construction": true});
            skPoint(sketch, "E106.visualSharp", {"position": v(0, 304.8) * mm});
            skPoint(sketch, "E107.visualSharp", {"position": v(406.4, 304.8) * mm});
            skArc(sketch, "E107.filletArc", {"start": v(406.4, 254) * mm, "mid": v(391.52, 289.92) * mm, "end": v(355.6, 304.8) * mm});
            skPoint(sketch, "E108.visualSharp", {"position": v(406.4, 0) * mm});
            skPoint(sketch, "E109.visualSharp", {"position": v(0, 0) * mm});
            skLineSegment(sketch, "E110", {"start": v(102.87, 292.1) * mm, "end": v(102.87, 241.3) * mm});
            skLineSegment(sketch, "E111", {"start": v(115.57, 228.6) * mm, "end": v(182.25, 228.6) * mm});
            skLineSegment(sketch, "E112", {"start": v(194.94, 215.9) * mm, "end": v(194.94, 179.39) * mm});
            skLineSegment(sketch, "E113", {"start": v(207.65, 166.69) * mm, "end": v(287.02, 166.69) * mm});
            skLineSegment(sketch, "E114", {"start": v(299.72, 153.99) * mm, "end": v(299.72, 132.44) * mm});
            skLineSegment(sketch, "E115", {"start": v(83.82, 152.4) * mm, "end": v(102.87, 152.4) * mm, "construction": true});
            skLineSegment(sketch, "E116", {"start": v(102.87, 152.4) * mm, "end": v(121.92, 152.4) * mm, "construction": true});
            skLineSegment(sketch, "E117", {"start": v(172.72, 114.3) * mm, "end": v(194.94, 114.3) * mm, "construction": true});
            skLineSegment(sketch, "E118", {"start": v(194.94, 114.3) * mm, "end": v(217.17, 114.3) * mm, "construction": true});
            skLineSegment(sketch, "E119", {"start": v(274.32, 66.67) * mm, "end": v(299.72, 66.67) * mm, "construction": true});
            skLineSegment(sketch, "E120", {"start": v(299.72, 66.67) * mm, "end": v(325.12, 66.67) * mm, "construction": true});
            skLineSegment(sketch, "E121", {"start": v(147.32, 241.3) * mm, "end": v(147.32, 215.9) * mm, "construction": true});
            skLineSegment(sketch, "E122", {"start": v(245.74, 152.4) * mm, "end": v(245.74, 180.97) * mm, "construction": true});
            skPoint(sketch, "E123.visualSharp", {"position": v(299.72, 166.69) * mm});
            skArc(sketch, "E123.filletArc", {"start": v(299.72, 153.99) * mm, "mid": v(296, 162.97) * mm, "end": v(287.02, 166.69) * mm});
            skPoint(sketch, "E124.visualSharp", {"position": v(194.94, 166.69) * mm});
            skArc(sketch, "E124.filletArc", {"start": v(194.94, 179.39) * mm, "mid": v(198.66, 170.4) * mm, "end": v(207.65, 166.69) * mm});
            skPoint(sketch, "E125.visualSharp", {"position": v(194.94, 228.6) * mm});
            skArc(sketch, "E125.filletArc", {"start": v(194.94, 215.9) * mm, "mid": v(191.23, 224.88) * mm, "end": v(182.25, 228.6) * mm});
            skPoint(sketch, "E126.visualSharp", {"position": v(102.87, 228.6) * mm});
            skArc(sketch, "E126.filletArc", {"start": v(102.87, 241.3) * mm, "mid": v(106.59, 232.32) * mm, "end": v(115.57, 228.6) * mm});
            skArc(sketch, "E127.filletArc", {"start": v(115.57, 304.8) * mm, "mid": v(106.59, 301.08) * mm, "end": v(102.87, 292.1) * mm});
            skPoint(sketch, "E128", {"position": v(147.32, 228.6) * mm});
            skPoint(sketch, "E129", {"position": v(245.74, 166.69) * mm});
            skLineSegment(sketch, "E130", {"start": v(393.7, 119.74) * mm, "end": v(312.42, 119.74) * mm});
            skLineSegment(sketch, "E131", {"start": v(325.12, 136.07) * mm, "end": v(325.12, 103.41) * mm});
            skPoint(sketch, "E132", {"position": v(325.12, 119.74) * mm});
            skArc(sketch, "E133.filletArc", {"start": v(299.72, 132.44) * mm, "mid": v(303.44, 123.46) * mm, "end": v(312.42, 119.74) * mm});
            skArc(sketch, "E134.filletArc", {"start": v(393.7, 119.74) * mm, "mid": v(402.68, 123.46) * mm, "end": v(406.4, 132.44) * mm});
            skCircle(sketch, "E135.0", {"center": v(50.8, 285.75) * mm, "radius": 1.65 * mm, "construction": true});
            skCircle(sketch, "E135.1", {"center": v(387.35, 50.8) * mm, "radius": 1.65 * mm, "construction": true});
            skCircle(sketch, "E136", {"center": v(121.92, 285.75) * mm, "radius": 1.65 * mm});
            skCircle(sketch, "E137", {"center": v(194.94, 241.3) * mm, "radius": 1.65 * mm});
            skCircle(sketch, "E138", {"center": v(299.72, 179.39) * mm, "radius": 1.65 * mm});
            skCircle(sketch, "E139", {"center": v(387.35, 138.8) * mm, "radius": 1.65 * mm});
            skLineSegment(sketch, "E140", {"start": v(387.35, 119.74) * mm, "end": v(387.35, 138.8) * mm, "construction": true});
            skLineSegment(sketch, "E141", {"start": v(387.35, 138.8) * mm, "end": v(406.4, 138.8) * mm, "construction": true});
            skLineSegment(sketch, "E142", {"start": v(299.72, 166.69) * mm, "end": v(299.72, 179.39) * mm, "construction": true});
            skLineSegment(sketch, "E143", {"start": v(194.94, 228.6) * mm, "end": v(194.94, 241.3) * mm, "construction": true});
            skLineSegment(sketch, "E144", {"start": v(121.92, 285.75) * mm, "end": v(121.92, 304.8) * mm, "construction": true});
            skLineSegment(sketch, "E145", {"start": v(102.87, 285.75) * mm, "end": v(121.92, 285.75) * mm, "construction": true});
            skLineSegment(sketch, "E146.0", {"start": v(102.87, 163.83) * mm, "end": v(102.87, 176.53) * mm, "construction": true});
            skSolve(sketch);
        }
        {
            var Q0;
            Q0 = qSketchRegion(id + "F5", true);
            extrude(context, id + "F7", {"entities" : qUnion([Q0]), "operationType" : NewBodyOperationType.INTERSECT, "endBound" : BoundingType.THROUGH_ALL, "depth" : 25.4 * mm, "offsetDistance" : 25.4 * mm});
        }
        {
            var Q0;
            Q0 = qSketchRegion(id + "F6", true);
            extrude(context, id + "F8", {"entities" : qUnion([Q0]), "operationType" : NewBodyOperationType.INTERSECT, "endBound" : BoundingType.THROUGH_ALL, "depth" : 25.4 * mm, "offsetDistance" : 25.4 * mm});
        }
        {
            var Q0;
            Q0=makeQuery(id+"F5.imprint","IMPRINT",FACE,{"disambiguationData":[TD([[makeQuery(id+"F5.imprint","IMPRINT",EDGE,{"derivedFrom":sQuery(id+"F5.wireOp",EDGE,"E86")}),1.0]])]});
            var Q1;
            Q1=makeQuery(id+"F5.imprint","IMPRINT",FACE,{"disambiguationData":[TD([[makeQuery(id+"F5.imprint","IMPRINT",EDGE,{"derivedFrom":sQuery(id+"F5.wireOp",EDGE,"E79")}),1.0]])]});
            var Q2;
            Q2=makeQuery(id+"F5.imprint","IMPRINT",FACE,{"disambiguationData":[TD([[makeQuery(id+"F5.imprint","IMPRINT",EDGE,{"derivedFrom":sQuery(id+"F5.wireOp",EDGE,"E80")}),1.0]])]});
            var Q3;
            Q3=makeQuery(id+"F5.imprint","IMPRINT",FACE,{"disambiguationData":[TD([[makeQuery(id+"F5.imprint","IMPRINT",EDGE,{"derivedFrom":sQuery(id+"F5.wireOp",EDGE,"E81")}),1.0]])]});
            var Q4;
            Q4=makeQuery(id+"F5.imprint","IMPRINT",FACE,{"disambiguationData":[TD([[makeQuery(id+"F5.imprint","IMPRINT",EDGE,{"derivedFrom":sQuery(id+"F5.wireOp",EDGE,"E90")}),1.0]])]});
            var Q5;
            Q5=makeQuery(id+"F6.imprint","IMPRINT",FACE,{"disambiguationData":[TD([[makeQuery(id+"F6.imprint","IMPRINT",EDGE,{"derivedFrom":sQuery(id+"F6.wireOp",EDGE,"E136")}),1.0]])]});
            var Q6;
            Q6=makeQuery(id+"F6.imprint","IMPRINT",FACE,{"disambiguationData":[TD([[makeQuery(id+"F6.imprint","IMPRINT",EDGE,{"derivedFrom":sQuery(id+"F6.wireOp",EDGE,"E137")}),1.0]])]});
            var Q7;
            Q7=makeQuery(id+"F6.imprint","IMPRINT",FACE,{"disambiguationData":[TD([[makeQuery(id+"F6.imprint","IMPRINT",EDGE,{"derivedFrom":sQuery(id+"F6.wireOp",EDGE,"E138")}),1.0]])]});
            var Q8;
            Q8=makeQuery(id+"F6.imprint","IMPRINT",FACE,{"disambiguationData":[TD([[makeQuery(id+"F6.imprint","IMPRINT",EDGE,{"derivedFrom":sQuery(id+"F6.wireOp",EDGE,"E139")}),1.0]])]});
            extrude(context, id + "F9", {"entities" : qUnion([Q0, Q1, Q2, Q3, Q4, Q5, Q6, Q7, Q8]), "operationType" : NewBodyOperationType.REMOVE, "endBound" : BoundingType.SYMMETRIC, "oppositeDirection" : true, "depth" : 304.8 * mm, "offsetDistance" : 25.4 * mm});
        }
    });
